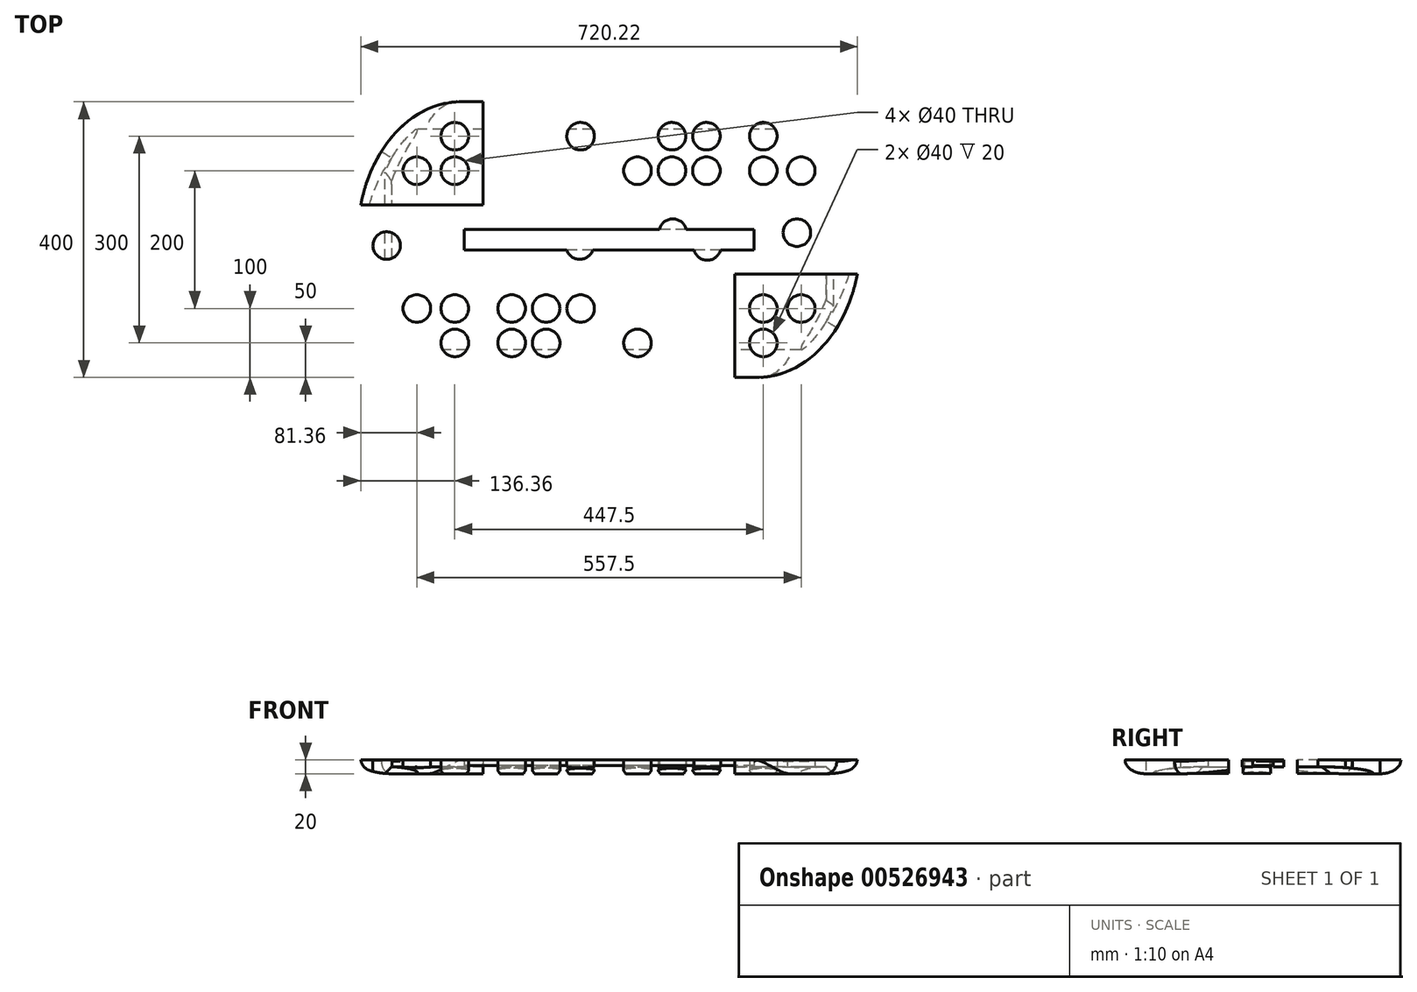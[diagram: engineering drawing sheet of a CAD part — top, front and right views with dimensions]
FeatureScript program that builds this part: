
annotation { "Feature Type Name" : "Feature", "Feature Type Description" : "" }
export const myFeature = defineFeature(function(context is Context, id is Id, definition is map)
    precondition{}
    {
        {
            var Q0;
            Q0=qCreatedBy(makeId("Top.planeOp"),FACE);
            var sketch = newSketch(context, id + "F0", { "sketchPlane" : qUnion([Q0])});
            skLineSegment(sketch, "E0.bottom", {"start": v(-365, 200) * mm, "end": v(365, 200) * mm});
            skLineSegment(sketch, "E0.top", {"start": v(-365, -200) * mm, "end": v(365, -200) * mm});
            skLineSegment(sketch, "E0.left", {"start": v(-365, 200) * mm, "end": v(-365, -200) * mm});
            skLineSegment(sketch, "E0.right", {"start": v(365, 200) * mm, "end": v(365, -200) * mm});
            skPoint(sketch, "E0.middle", {"position": v(0, 0) * mm});
            skEllipticalArc(sketch, "E1", {});
            skEllipticalArc(sketch, "E2.MirrorCS", {});
            skEllipticalArc(sketch, "E3.MirrorCS", {});
            skEllipticalArc(sketch, "E4.MirrorCS", {});
            skLineSegment(sketch, "E5", {"start": v(-365, 200) * mm, "end": v(-105, 200) * mm});
            skLineSegment(sketch, "E6", {"start": v(-365, 200) * mm, "end": v(-365, 50) * mm});
            skLineSegment(sketch, "E7", {"start": v(-365, -200) * mm, "end": v(-365, -50) * mm});
            skLineSegment(sketch, "E8", {"start": v(-365, -200) * mm, "end": v(-182.5, -200) * mm});
            skLineSegment(sketch, "E9", {"start": v(365, 200) * mm, "end": v(105, 200) * mm});
            skLineSegment(sketch, "E10", {"start": v(182.5, -200.11) * mm, "end": v(365, -200) * mm});
            skPoint(sketch, "E11", {"position": v(0, 200) * mm});
            skLineSegment(sketch, "E12", {"start": v(0, 200) * mm, "end": v(-130, 200) * mm});
            skLineSegment(sketch, "E13.MirrorCS", {"start": v(0, -200) * mm, "end": v(-130, -200) * mm});
            skLineSegment(sketch, "E14.MirrorCS", {"start": v(5, 200) * mm, "end": v(130, 200) * mm});
            skLineSegment(sketch, "E15.MirrorCS", {"start": v(-72.5, -200) * mm, "end": v(52.5, -200) * mm});
            skCircle(sketch, "E16", {"center": v(-278.75, 100) * mm, "radius": 20 * mm});
            skCircle(sketch, "E17", {"center": v(-223.75, 150) * mm, "radius": 20 * mm});
            skCircle(sketch, "E18", {"center": v(-223.75, 100) * mm, "radius": 20 * mm});
            skCircle(sketch, "E19", {"center": v(-141.25, 100) * mm, "radius": 20 * mm});
            skCircle(sketch, "E20", {"center": v(-141.25, 150) * mm, "radius": 20 * mm});
            skCircle(sketch, "E21", {"center": v(-91.25, 100) * mm, "radius": 20 * mm});
            skCircle(sketch, "E22", {"center": v(-91.25, 150) * mm, "radius": 20 * mm});
            skCircle(sketch, "E23", {"center": v(-41.25, 100) * mm, "radius": 20 * mm});
            skCircle(sketch, "E24.MirrorC", {"center": v(-41.25, 150) * mm, "radius": 20 * mm});
            skCircle(sketch, "E25.MirrorC", {"center": v(-278.75, -100) * mm, "radius": 20 * mm});
            skCircle(sketch, "E26.MirrorC", {"center": v(-223.75, -150) * mm, "radius": 20 * mm});
            skCircle(sketch, "E27.MirrorC", {"center": v(-223.75, -100) * mm, "radius": 20 * mm});
            skCircle(sketch, "E28.MirrorC", {"center": v(-141.25, -100) * mm, "radius": 20 * mm});
            skCircle(sketch, "E29.MirrorC", {"center": v(-141.25, -150) * mm, "radius": 20 * mm});
            skCircle(sketch, "E30.MirrorC", {"center": v(-91.25, -100) * mm, "radius": 20 * mm});
            skCircle(sketch, "E31.MirrorC", {"center": v(-41.25, -100) * mm, "radius": 20 * mm});
            skCircle(sketch, "E32.MirrorC", {"center": v(-91.25, -150) * mm, "radius": 20 * mm});
            skCircle(sketch, "E33.MirrorC", {"center": v(-41.25, -150) * mm, "radius": 20 * mm});
            skCircle(sketch, "E34.MirrorC", {"center": v(-222.5, -10) * mm, "radius": 20 * mm});
            skLineSegment(sketch, "E35.bottom", {"start": v(210, 15) * mm, "end": v(-210, 15) * mm});
            skLineSegment(sketch, "E35.top", {"start": v(210, -15) * mm, "end": v(-210, -15) * mm});
            skLineSegment(sketch, "E35.left", {"start": v(210, 15) * mm, "end": v(210, -15) * mm});
            skLineSegment(sketch, "E35.right", {"start": v(-210, 15) * mm, "end": v(-210, -15) * mm});
            skLineSegment(sketch, "E36", {"start": v(-365, -50) * mm, "end": v(365, -50) * mm});
            skLineSegment(sketch, "E37", {"start": v(-365, 50) * mm, "end": v(365, 50) * mm});
            skLineSegment(sketch, "E38", {"start": v(-182.5, -200) * mm, "end": v(-182.5, -40.61) * mm});
            skLineSegment(sketch, "E39", {"start": v(0, -200) * mm, "end": v(0, -50) * mm});
            skLineSegment(sketch, "E40", {"start": v(182.5, -200.11) * mm, "end": v(182.4, -40.7) * mm});
            skLineSegment(sketch, "E41.trimOffspring", {"start": v(-182.5, 40.61) * mm, "end": v(-182.5, 200) * mm});
            skLineSegment(sketch, "E42.trimOffspring", {"start": v(-182.5, -15) * mm, "end": v(-182.5, 15) * mm});
            skLineSegment(sketch, "E43.trimOffspring", {"start": v(182.39, -15) * mm, "end": v(182.37, 15) * mm});
            skLineSegment(sketch, "E44.trimOffspring", {"start": v(182.35, 40.73) * mm, "end": v(182.25, 200) * mm});
            skCircle(sketch, "E45", {"center": v(-272.5, 10) * mm, "radius": 20 * mm});
            skCircle(sketch, "E46.MirrorC", {"center": v(-322.5, -8.74) * mm, "radius": 20 * mm});
            skCircle(sketch, "E47.MirrorC", {"center": v(-142.5, -10) * mm, "radius": 20 * mm});
            skCircle(sketch, "E48.MirrorC", {"center": v(-92.5, 10) * mm, "radius": 20 * mm});
            skCircle(sketch, "E49.MirrorC", {"center": v(-42.5, -8.74) * mm, "radius": 20 * mm});
            skCircle(sketch, "E50.MirrorC", {"center": v(42.5, -8.74) * mm, "radius": 20 * mm});
            skCircle(sketch, "E51.MirrorC", {"center": v(142.5, -10) * mm, "radius": 20 * mm});
            skCircle(sketch, "E52.MirrorC", {"center": v(92.5, 10) * mm, "radius": 20 * mm});
            skCircle(sketch, "E53.MirrorC", {"center": v(222.5, -10) * mm, "radius": 20 * mm});
            skCircle(sketch, "E54.MirrorC", {"center": v(272.5, 10) * mm, "radius": 20 * mm});
            skCircle(sketch, "E55.MirrorC", {"center": v(322.5, -8.74) * mm, "radius": 20 * mm});
            skCircle(sketch, "E56.MirrorC", {"center": v(223.75, -100) * mm, "radius": 20 * mm});
            skCircle(sketch, "E57.MirrorC", {"center": v(223.75, -150) * mm, "radius": 20 * mm});
            skCircle(sketch, "E58.MirrorC", {"center": v(278.75, -100) * mm, "radius": 20 * mm});
            skCircle(sketch, "E59.MirrorC", {"center": v(141.25, -100) * mm, "radius": 20 * mm});
            skCircle(sketch, "E60.MirrorC", {"center": v(141.25, -150) * mm, "radius": 20 * mm});
            skCircle(sketch, "E61.MirrorC", {"center": v(91.25, -150) * mm, "radius": 20 * mm});
            skCircle(sketch, "E62.MirrorC", {"center": v(91.25, -100) * mm, "radius": 20 * mm});
            skCircle(sketch, "E63.MirrorC", {"center": v(41.25, -100) * mm, "radius": 20 * mm});
            skCircle(sketch, "E64.MirrorC", {"center": v(41.25, -150) * mm, "radius": 20 * mm});
            skCircle(sketch, "E65.MirrorC", {"center": v(41.25, 100) * mm, "radius": 20 * mm});
            skCircle(sketch, "E66.MirrorC", {"center": v(91.25, 100) * mm, "radius": 20 * mm});
            skCircle(sketch, "E67.MirrorC", {"center": v(141.25, 100) * mm, "radius": 20 * mm});
            skCircle(sketch, "E68.MirrorC", {"center": v(223.75, 100) * mm, "radius": 20 * mm});
            skCircle(sketch, "E69.MirrorC", {"center": v(278.75, 100) * mm, "radius": 20 * mm});
            skCircle(sketch, "E70.MirrorC", {"center": v(223.75, 150) * mm, "radius": 20 * mm});
            skCircle(sketch, "E71.MirrorC", {"center": v(141.25, 150) * mm, "radius": 20 * mm});
            skCircle(sketch, "E72.MirrorC", {"center": v(91.25, 150) * mm, "radius": 20 * mm});
            skCircle(sketch, "E73.MirrorC", {"center": v(41.25, 150) * mm, "radius": 20 * mm});
            const initialGuessF0  = {"E1": [0.215000023161019, -0.00011114199246731203, 0, -1, 0.20000000103052606, 0.15, 6.249845643425636, 1.5707963267948966], "E2.MirrorCS": [-0.215, -0.00011114199246737072, 0, -1, 0.2, 0.15, 4.711833270393751, 0.03333950926130193], "E3.MirrorCS": [-0.215, 0.00011114199246727815, 0, 1, 0.2, 0.15, 6.249845797918284, 1.5707963267948966], "E4.MirrorCS": [0.215, 0.00011114199246735796, 0, 1, 0.2, 0.15, 4.711277560231201, 0.03333950926130226]};
            skSetInitialGuess(sketch, initialGuessF0);
            skSolve(sketch);
        }
        {
            var Q0;
            Q0=qCreatedBy(makeId("Top.planeOp"),FACE);
            cPlane(context, id + "F1", {"entities" : qUnion([Q0]), "cplaneType" : CPlaneType.OFFSET, "offset" : 20 * mm, "width" : 150 * mm, "height" : 150 * mm});
        }
        {
            var Q0;
            Q0=qCreatedBy(id+"F1.planeOp",FACE);
            var sketch = newSketch(context, id + "F2", { "sketchPlane" : qUnion([Q0])});
            skLineSegment(sketch, "E74.bottom", {"start": v(0, 0) * mm, "end": v(365, 0) * mm});
            skLineSegment(sketch, "E74.top", {"start": v(0, -200) * mm, "end": v(210, -200) * mm});
            skLineSegment(sketch, "E74.left", {"start": v(0, 0) * mm, "end": v(0, -200) * mm});
            skLineSegment(sketch, "E75", {"start": v(0, -15) * mm, "end": v(364.58, -15) * mm});
            skLineSegment(sketch, "E76", {"start": v(0, -170) * mm, "end": v(294.02, -170) * mm});
            skLineSegment(sketch, "E77", {"start": v(330, 0) * mm, "end": v(330, -128.4) * mm});
            skLineSegment(sketch, "E78", {"start": v(215, 0) * mm, "end": v(215, -200) * mm});
            skPoint(sketch, "E79", {"position": v(215, -200) * mm});
            skPoint(sketch, "E80", {"position": v(365, 0) * mm});
            skLineSegment(sketch, "E81", {"start": v(275, 0) * mm, "end": v(275, -183.3) * mm});
            skLineSegment(sketch, "E82", {"start": v(275, -140) * mm, "end": v(322.12, -140) * mm});
            skPoint(sketch, "E83", {"position": v(215, -170) * mm});
            skPoint(sketch, "E84", {"position": v(330, 0) * mm});
            skPoint(sketch, "E85", {"position": v(275, -140) * mm});
            skPoint(sketch, "E86", {"position": v(330, -140) * mm});
            skPoint(sketch, "E87", {"position": v(275, -185) * mm});
            skLineSegment(sketch, "E88", {"start": v(315, -149.07) * mm, "end": v(315, 0) * mm});
            skLineSegment(sketch, "E89", {"start": v(210, 0) * mm, "end": v(210, -200) * mm});
            skEllipticalArc(sketch, "E90.trimOffspring", {});
            skEllipticalArc(sketch, "E91", {});
            skPoint(sketch, "E92.orphan", {"position": v(365, -170) * mm});
            skPoint(sketch, "E93.trimOffspring.end.orphan", {"position": v(330, -200) * mm});
            skPoint(sketch, "E94.orphan", {"position": v(365, -200) * mm});
            skPoint(sketch, "E95.orphan", {"position": v(365, -15) * mm});
            skLineSegment(sketch, "E96.MirrorCS", {"start": v(0, 0) * mm, "end": v(-365, 0) * mm});
            skLineSegment(sketch, "E97.MirrorCS", {"start": v(0, -15) * mm, "end": v(-364.58, -15) * mm});
            skLineSegment(sketch, "E98.MirrorCS", {"start": v(0, -170) * mm, "end": v(-294.02, -170) * mm});
            skLineSegment(sketch, "E99.MirrorCS", {"start": v(0, -200) * mm, "end": v(-210, -200) * mm});
            skLineSegment(sketch, "E100.MirrorCS", {"start": v(-210, 0) * mm, "end": v(-210, -200) * mm});
            skLineSegment(sketch, "E101.MirrorCS", {"start": v(-215, 0) * mm, "end": v(-215, -200) * mm});
            skEllipticalArc(sketch, "E102.MirrorCS", {});
            skEllipticalArc(sketch, "E103.MirrorCS", {});
            skLineSegment(sketch, "E104.MirrorCS", {"start": v(-275, 0) * mm, "end": v(-275, -183.3) * mm});
            skLineSegment(sketch, "E105.MirrorCS", {"start": v(-275, -140) * mm, "end": v(-322.12, -140) * mm});
            skLineSegment(sketch, "E106.MirrorCS", {"start": v(-315, -149.07) * mm, "end": v(-315, 0) * mm});
            skLineSegment(sketch, "E107.MirrorCS", {"start": v(-330, 0) * mm, "end": v(-330, -128.4) * mm});
            skLineSegment(sketch, "E108.MirrorCS", {"start": v(0, 15) * mm, "end": v(-364.58, 15) * mm});
            skLineSegment(sketch, "E109.MirrorCS", {"start": v(0, 15) * mm, "end": v(364.58, 15) * mm});
            skEllipticalArc(sketch, "E110.MirrorCS", {});
            skLineSegment(sketch, "E111.MirrorCS", {"start": v(-330, 0) * mm, "end": v(-330, 128.4) * mm});
            skLineSegment(sketch, "E112.MirrorCS", {"start": v(-315, 149.07) * mm, "end": v(-315, 0) * mm});
            skLineSegment(sketch, "E113.MirrorCS", {"start": v(-275, 0) * mm, "end": v(-275, 183.3) * mm});
            skLineSegment(sketch, "E114.MirrorCS", {"start": v(-215, 0) * mm, "end": v(-215, 200) * mm});
            skLineSegment(sketch, "E115.MirrorCS", {"start": v(-210, 0) * mm, "end": v(-210, 200) * mm});
            skLineSegment(sketch, "E116.MirrorCS", {"start": v(0, 0) * mm, "end": v(0, 200) * mm});
            skLineSegment(sketch, "E117.MirrorCS", {"start": v(210, 0) * mm, "end": v(210, 200) * mm});
            skLineSegment(sketch, "E118.MirrorCS", {"start": v(215, 0) * mm, "end": v(215, 200) * mm});
            skLineSegment(sketch, "E119.MirrorCS", {"start": v(275, 0) * mm, "end": v(275, 183.3) * mm});
            skLineSegment(sketch, "E120.MirrorCS", {"start": v(315, 149.07) * mm, "end": v(315, 0) * mm});
            skLineSegment(sketch, "E121.MirrorCS", {"start": v(330, 0) * mm, "end": v(330, 128.4) * mm});
            skEllipticalArc(sketch, "E122.MirrorCS", {});
            skEllipticalArc(sketch, "E123.MirrorCS", {});
            skEllipticalArc(sketch, "E124.MirrorCS", {});
            skLineSegment(sketch, "E125.MirrorCS", {"start": v(-275, 140) * mm, "end": v(-322.12, 140) * mm});
            skLineSegment(sketch, "E126.MirrorCS", {"start": v(0, 170) * mm, "end": v(-294.02, 170) * mm});
            skLineSegment(sketch, "E127.MirrorCS", {"start": v(0, 170) * mm, "end": v(294.02, 170) * mm});
            skLineSegment(sketch, "E128.MirrorCS", {"start": v(0, 200) * mm, "end": v(210, 200) * mm});
            skLineSegment(sketch, "E129.MirrorCS", {"start": v(0, 200) * mm, "end": v(-210, 200) * mm});
            skLineSegment(sketch, "E130.MirrorCS", {"start": v(275, 140) * mm, "end": v(322.12, 140) * mm});
            const initialGuessF2  = {"E90.trimOffspring": [0.215, 0, 1, 0, 0.115, 0.17, 4.71238898038469, 6.283185307179586], "E91": [0.215, 0, 0, -1, 0.2, 0.15, 6.249845797918284, 1.5707963267948966], "E102.MirrorCS": [-0.215, 0, -1, 0, 0.115, 0.17, 6.283185307179586, 1.5707963267948966], "E103.MirrorCS": [-0.215, 0, 0, -1, 0.2, 0.15, 4.71238898038469, 0.03333950926130225], "E110.MirrorCS": [-0.215, 0, 0, 1, 0.2, 0.15, 6.249845797918284, 1.5707963267948966], "E122.MirrorCS": [0.215, 0, 0, 1, 0.2, 0.15, 4.71238898038469, 0.03333950926130225], "E123.MirrorCS": [0.215, 0, 1, 0, 0.115, 0.17, 6.283185307179586, 1.5707963267948966], "E124.MirrorCS": [-0.215, 0, -1, 0, 0.115, 0.17, 4.71238898038469, 6.283185307179586]};
            skSetInitialGuess(sketch, initialGuessF2);
            skSolve(sketch);
        }
        {
            var Q0;
            Q0=qCreatedBy(makeId("Right.planeOp"),FACE);
            var sketch = newSketch(context, id + "F3", { "sketchPlane" : qUnion([Q0])});
            skPoint(sketch, "E131.middle", {"position": v(0, 20) * mm});
            skPoint(sketch, "E132", {"position": v(170, 0) * mm});
            skPoint(sketch, "E133", {"position": v(160, 0) * mm});
            skLineSegment(sketch, "E134.bottom", {"start": v(15, 10.07) * mm, "end": v(80, 10.07) * mm});
            skPoint(sketch, "E135", {"position": v(80, 10.07) * mm});
            skEllipticalArc(sketch, "E136", {});
            skEllipticalArc(sketch, "E137", {});
            skLineSegment(sketch, "E138", {"start": v(0, 20) * mm, "end": v(0, 10.04) * mm});
            skLineSegment(sketch, "E139", {"start": v(0, 20) * mm, "end": v(200, 20) * mm});
            skLineSegment(sketch, "E140", {"start": v(200, 20) * mm, "end": v(0, 20) * mm});
            skLineSegment(sketch, "E141", {"start": v(160, 0) * mm, "end": v(170, 0) * mm});
            skPoint(sketch, "E142.orphan", {"position": v(-200, 20) * mm});
            skLineSegment(sketch, "E143.MirrorCS", {"start": v(-200, 20) * mm, "end": v(0, 20) * mm});
            skLineSegment(sketch, "E144.MirrorCS", {"start": v(-15, 10.07) * mm, "end": v(-80, 10.07) * mm});
            skEllipticalArc(sketch, "E145.MirrorCS", {});
            skLineSegment(sketch, "E146.MirrorCS", {"start": v(-160, 0) * mm, "end": v(-170, 0) * mm});
            skEllipticalArc(sketch, "E147.MirrorCS", {});
            skLineSegment(sketch, "E148.top", {"start": v(-15, 12) * mm, "end": v(15, 12) * mm});
            skLineSegment(sketch, "E148.left", {"start": v(-15, 10.07) * mm, "end": v(-15, 12) * mm});
            skLineSegment(sketch, "E148.right", {"start": v(15, 10.07) * mm, "end": v(15, 12) * mm});
            skLineSegment(sketch, "E149.bottom", {"start": v(15, 18) * mm, "end": v(-15, 18) * mm});
            skLineSegment(sketch, "E149.top", {"start": v(15, 12) * mm, "end": v(-15, 12) * mm});
            skLineSegment(sketch, "E149.left", {"start": v(15, 18) * mm, "end": v(15, 12) * mm});
            skLineSegment(sketch, "E149.right", {"start": v(-15, 18) * mm, "end": v(-15, 12) * mm});
            skLineSegment(sketch, "E150", {"start": v(170, 0) * mm, "end": v(170.12, 20) * mm});
            skLineSegment(sketch, "E151", {"start": v(-170, 0) * mm, "end": v(-170.12, 20) * mm});
            skLineSegment(sketch, "E152", {"start": v(-15, 12) * mm, "end": v(-15, 10.07) * mm});
            skLineSegment(sketch, "E153.bottom", {"start": v(-200, 20) * mm, "end": v(-170, 20) * mm});
            skLineSegment(sketch, "E153.top", {"start": v(-200, 0) * mm, "end": v(-170, 0) * mm});
            skLineSegment(sketch, "E153.left", {"start": v(-200, 20) * mm, "end": v(-200, 0) * mm});
            skLineSegment(sketch, "E153.right", {"start": v(-170, 20) * mm, "end": v(-170, 0) * mm});
            skLineSegment(sketch, "E154.MirrorCS", {"start": v(200, 0) * mm, "end": v(170, 0) * mm});
            skLineSegment(sketch, "E155.MirrorCS", {"start": v(200, 20) * mm, "end": v(200, 0) * mm});
            skLineSegment(sketch, "E156", {"start": v(80, 10.07) * mm, "end": v(80, 20) * mm});
            skLineSegment(sketch, "E157", {"start": v(160, 0) * mm, "end": v(160, 20) * mm});
            skLineSegment(sketch, "E158", {"start": v(149.2, 20) * mm, "end": v(149.2, 5.05) * mm});
            skLineSegment(sketch, "E159", {"start": v(140.08, 20) * mm, "end": v(140.08, 6.65) * mm});
            skLineSegment(sketch, "E160", {"start": v(128.23, 20) * mm, "end": v(128.23, 8.04) * mm});
            skLineSegment(sketch, "E161", {"start": v(102.69, 20) * mm, "end": v(102.69, 9.66) * mm});
            skLineSegment(sketch, "E162.MirrorCS", {"start": v(-80, 10.07) * mm, "end": v(-80, 20) * mm});
            skLineSegment(sketch, "E163.MirrorCS", {"start": v(-102.69, 20) * mm, "end": v(-102.69, 9.66) * mm});
            skLineSegment(sketch, "E164.MirrorCS", {"start": v(-128.23, 20) * mm, "end": v(-128.23, 8.04) * mm});
            skLineSegment(sketch, "E165.MirrorCS", {"start": v(-140.08, 20) * mm, "end": v(-140.08, 6.65) * mm});
            skLineSegment(sketch, "E166.MirrorCS", {"start": v(-149.2, 20) * mm, "end": v(-149.2, 5.05) * mm});
            skLineSegment(sketch, "E167.MirrorCS", {"start": v(-160, 0) * mm, "end": v(-160, 20) * mm});
            skLineSegment(sketch, "E168", {"start": v(45, 20) * mm, "end": v(45, 10.07) * mm});
            skLineSegment(sketch, "E169.MirrorCS", {"start": v(-45, 20) * mm, "end": v(-45, 10.07) * mm});
            const initialGuessF3  = {"E136": [0.17012490332126617, 0.02, -0.006245044279577429, -0.9999804995208388, 0.020000390017188747, 0.02987581400604767, 6.283185307179586, 1.580124845260153], "E137": [0.08, 0, 0, 1, 0.01007139225942586, 0.08, 4.71238898038469, 6.283185307179586], "E145.MirrorCS": [-0.08, 0, 0, 1, 0.01007139225942586, 0.08, 6.283185307179586, 1.5707963267948966], "E147.MirrorCS": [-0.17012490332126617, 0.02, 0.006245044279579518, -0.9999804995208388, 0.020000390017188747, 0.02987581400604767, 4.703060461919433, 6.283185307179586]};
            skSetInitialGuess(sketch, initialGuessF3);
            skSolve(sketch);
        }
        {
            var Q0;
            Q0=qCreatedBy(makeId("Front.planeOp"),FACE);
            var sketch = newSketch(context, id + "F4", { "sketchPlane" : qUnion([Q0])});
            skLineSegment(sketch, "E170", {"start": v(0, 20) * mm, "end": v(365, 20) * mm});
            skPoint(sketch, "E171", {"position": v(210, 20) * mm});
            skLineSegment(sketch, "E172", {"start": v(210, 18) * mm, "end": v(210, 12) * mm});
            skPoint(sketch, "E173", {"position": v(315, 20) * mm});
            skLineSegment(sketch, "E174", {"start": v(315, 18) * mm, "end": v(315, 0) * mm});
            skLineSegment(sketch, "E175", {"start": v(0, 12) * mm, "end": v(0, 20) * mm});
            skLineSegment(sketch, "E176", {"start": v(210, 12) * mm, "end": v(0, 12) * mm});
            skPoint(sketch, "E177", {"position": v(365.07, 0) * mm});
            skPoint(sketch, "E178", {"position": v(365, 20) * mm});
            skEllipticalArc(sketch, "E179", {});
            skLineSegment(sketch, "E180", {"start": v(315, 18) * mm, "end": v(210, 18) * mm});
            skLineSegment(sketch, "E181.MirrorCS", {"start": v(0, 20) * mm, "end": v(-365, 20) * mm});
            skLineSegment(sketch, "E182.MirrorCS", {"start": v(-210, 12) * mm, "end": v(0, 12) * mm});
            skLineSegment(sketch, "E183.MirrorCS", {"start": v(-210, 18) * mm, "end": v(-210, 12) * mm});
            skLineSegment(sketch, "E184.MirrorCS", {"start": v(-315, 18) * mm, "end": v(-210, 18) * mm});
            skLineSegment(sketch, "E185.MirrorCS", {"start": v(-315, 18) * mm, "end": v(-315, 0) * mm});
            skEllipticalArc(sketch, "E186.MirrorCS", {});
            skPoint(sketch, "E187", {"position": v(245, 20) * mm});
            skPoint(sketch, "E188", {"position": v(245, 10.07) * mm});
            skPoint(sketch, "E189", {"position": v(325, 20) * mm});
            skPoint(sketch, "E190", {"position": v(335, 20) * mm});
            skLineSegment(sketch, "E191", {"start": v(335, 20) * mm, "end": v(335, 10.07) * mm});
            skLineSegment(sketch, "E192", {"start": v(335, 10.07) * mm, "end": v(0, 10.07) * mm});
            skLineSegment(sketch, "E193.MirrorCS", {"start": v(-335, 10.07) * mm, "end": v(0, 10.07) * mm});
            skLineSegment(sketch, "E194.MirrorCS", {"start": v(-335, 20) * mm, "end": v(-335, 10.07) * mm});
            skLineSegment(sketch, "E195", {"start": v(365, 20) * mm, "end": v(365.07, 0) * mm});
            skLineSegment(sketch, "E196", {"start": v(315, 0) * mm, "end": v(365.07, 0) * mm});
            skLineSegment(sketch, "E197.MirrorCS", {"start": v(-365, 20) * mm, "end": v(-365.07, 0) * mm});
            skLineSegment(sketch, "E198.MirrorCS", {"start": v(-315, 0) * mm, "end": v(-365.07, 0) * mm});
            skLineSegment(sketch, "E199", {"start": v(335, 10.07) * mm, "end": v(335, 1.67) * mm});
            skLineSegment(sketch, "E200.MirrorCS", {"start": v(-335, 10.07) * mm, "end": v(-335, 1.67) * mm});
            skLineSegment(sketch, "E201", {"start": v(-315, 18) * mm, "end": v(-315, 20) * mm});
            skLineSegment(sketch, "E202", {"start": v(-210, 18) * mm, "end": v(-210, 20) * mm});
            skLineSegment(sketch, "E203.MirrorCS", {"start": v(210, 18) * mm, "end": v(210, 20) * mm});
            skLineSegment(sketch, "E204.MirrorCS", {"start": v(315, 18) * mm, "end": v(315, 20) * mm});
            skPoint(sketch, "E205", {"position": v(275, 20) * mm});
            skPoint(sketch, "E206.MirrorP", {"position": v(-275, 20) * mm});
            skLineSegment(sketch, "E207", {"start": v(275, 20) * mm, "end": v(275, 18) * mm});
            skLineSegment(sketch, "E208.MirrorCS", {"start": v(-275, 20) * mm, "end": v(-275, 18) * mm});
            skPoint(sketch, "E209", {"position": v(-333.25, 14.9) * mm});
            skPoint(sketch, "E210", {"position": v(-218.12, 14.9) * mm});
            skPoint(sketch, "E211", {"position": v(-78.75, 14.9) * mm});
            const initialGuessF4  = {"E179": [0.315, 0.02, 1, 0, 0.05, 0.02, 4.71238898038469, 0], "E186.MirrorCS": [-0.315, 0.02, -1, 0, 0.05, 0.02, 0, 1.5707963267948966]};
            skSetInitialGuess(sketch, initialGuessF4);
            skSolve(sketch);
        }
        {
            var Q0;
            Q0 = qSketchRegion(id + "F2", true);
            var Q1;
            {var subQ0=sQuery(id+"F2.wireOp",EDGE,"E125.MirrorCS");var subQ1=sQuery(id+"F2.wireOp",EDGE,"E112.MirrorCS");var subQ2=makeQuery(id+"F2.imprint","INTERSECT",VERTEX,{"derivedFrom":[subQ1,subQ0]});Q1=makeQuery(id+"F2.imprint","IMPRINT",FACE,{"disambiguationData":[TD([[makeQuery(id+"F2.imprint","IMPRINT",EDGE,{"disambiguationData":[TD([[subQ2,-1.0]])],"derivedFrom":subQ1}),1.0]])]});}
            var Q2;
            {var subQ0=sQuery(id+"F2.wireOp",EDGE,"E124.MirrorCS");var subQ1=sQuery(id+"F2.wireOp",EDGE,"E113.MirrorCS");var subQ2=makeQuery(id+"F2.imprint","INTERSECT",VERTEX,{"derivedFrom":[subQ1,subQ0]});Q2=makeQuery(id+"F2.imprint","IMPRINT",FACE,{"disambiguationData":[TD([[makeQuery(id+"F2.imprint","IMPRINT",EDGE,{"disambiguationData":[TD([[subQ2,-1.0]])],"derivedFrom":subQ1}),-1.0]])]});}
            var Q3;
            {var subQ0=sQuery(id+"F2.wireOp",EDGE,"E123.MirrorCS");var subQ1=sQuery(id+"F2.wireOp",EDGE,"E119.MirrorCS");var subQ2=makeQuery(id+"F2.imprint","INTERSECT",VERTEX,{"derivedFrom":[subQ1,subQ0]});Q3=makeQuery(id+"F2.imprint","IMPRINT",FACE,{"disambiguationData":[TD([[makeQuery(id+"F2.imprint","IMPRINT",EDGE,{"disambiguationData":[TD([[subQ2,-1.0]])],"derivedFrom":subQ1}),1.0]])]});}
            var Q4;
            {var subQ0=sQuery(id+"F2.wireOp",EDGE,"E130.MirrorCS");var subQ1=sQuery(id+"F2.wireOp",EDGE,"E120.MirrorCS");var subQ2=makeQuery(id+"F2.imprint","INTERSECT",VERTEX,{"derivedFrom":[subQ1,subQ0]});Q4=makeQuery(id+"F2.imprint","IMPRINT",FACE,{"disambiguationData":[TD([[makeQuery(id+"F2.imprint","IMPRINT",EDGE,{"disambiguationData":[TD([[subQ2,-1.0]])],"derivedFrom":subQ1}),-1.0]])]});}
            var Q5;
            {var subQ0=sQuery(id+"F2.wireOp",EDGE,"E90.trimOffspring");var subQ1=sQuery(id+"F2.wireOp",EDGE,"E82");var subQ2=makeQuery(id+"F2.imprint","INTERSECT",VERTEX,{"derivedFrom":[subQ1,subQ0]});Q5=makeQuery(id+"F2.imprint","IMPRINT",FACE,{"disambiguationData":[TD([[makeQuery(id+"F2.imprint","IMPRINT",EDGE,{"disambiguationData":[TD([[subQ2,-1.0]])],"derivedFrom":subQ1}),1.0]])]});}
            var Q6;
            {var subQ1=sQuery(id+"F2.wireOp",EDGE,"E76");var subQ3=sQuery(id+"F2.wireOp",EDGE,"E81");var subQ4=makeQuery(id+"F2.imprint","INTERSECT",VERTEX,{"derivedFrom":[subQ1,subQ3]});Q6=makeQuery(id+"F2.imprint","IMPRINT",FACE,{"disambiguationData":[TD([[makeQuery(id+"F2.imprint","IMPRINT",EDGE,{"disambiguationData":[TD([[subQ4,1.0]])],"derivedFrom":subQ3}),-1.0]])]});}
            var Q7;
            {var subQ1=sQuery(id+"F2.wireOp",EDGE,"E98.MirrorCS");var subQ3=sQuery(id+"F2.wireOp",EDGE,"E104.MirrorCS");var subQ4=makeQuery(id+"F2.imprint","INTERSECT",VERTEX,{"derivedFrom":[subQ1,subQ3]});Q7=makeQuery(id+"F2.imprint","IMPRINT",FACE,{"disambiguationData":[TD([[makeQuery(id+"F2.imprint","IMPRINT",EDGE,{"disambiguationData":[TD([[subQ4,1.0]])],"derivedFrom":subQ3}),1.0]])]});}
            var Q8;
            {var subQ0=sQuery(id+"F2.wireOp",EDGE,"E106.MirrorCS");var subQ1=sQuery(id+"F2.wireOp",EDGE,"E102.MirrorCS");var subQ2=makeQuery(id+"F2.imprint","INTERSECT",VERTEX,{"derivedFrom":[subQ1,subQ0]});Q8=makeQuery(id+"F2.imprint","IMPRINT",FACE,{"disambiguationData":[TD([[makeQuery(id+"F2.imprint","IMPRINT",EDGE,{"disambiguationData":[TD([[subQ2,-1.0]])],"derivedFrom":subQ1}),-1.0]])]});}
            extrude(context, id + "F5", {"entities" : qUnion([Q0, Q1, Q2, Q3, Q4, Q5, Q6, Q7, Q8]), "oppositeDirection" : true, "depth" : 20 * mm, "offsetDistance" : 25 * mm});
        }
        {
            var Q0;
            {var subQ0=sQuery(id+"F3.wireOp",EDGE,"E149.right");Q0=makeQuery(id+"F3.imprint","IMPRINT",FACE,{"disambiguationData":[TD([[makeQuery(id+"F3.imprint","IMPRINT",EDGE,{"derivedFrom":subQ0}),-1.0]])]});}
            var Q1;
            {var subQ0=sQuery(id+"F3.wireOp",EDGE,"E149.left");Q1=makeQuery(id+"F3.imprint","IMPRINT",FACE,{"disambiguationData":[TD([[makeQuery(id+"F3.imprint","IMPRINT",EDGE,{"derivedFrom":subQ0}),1.0]])]});}
            extrude(context, id + "F6", {"entities" : qUnion([Q0, Q1]), "operationType" : NewBodyOperationType.ADD, "depth" : 420 * mm, "offsetDistance" : 25 * mm, "symmetric" : true});
        }
        {
            var Q0;
            {var subQ0=sQuery(id+"F3.wireOp",EDGE,"E156");Q0=makeQuery(id+"F3.imprint","IMPRINT",FACE,{"disambiguationData":[TD([[makeQuery(id+"F3.imprint","IMPRINT",EDGE,{"derivedFrom":subQ0}),-1.0]])]});}
            var Q1;
            {var subQ0=sQuery(id+"F3.wireOp",EDGE,"E160");Q1=makeQuery(id+"F3.imprint","IMPRINT",FACE,{"disambiguationData":[TD([[makeQuery(id+"F3.imprint","IMPRINT",EDGE,{"derivedFrom":subQ0}),-1.0]])]});}
            var Q2;
            {var subQ0=sQuery(id+"F3.wireOp",EDGE,"E159");Q2=makeQuery(id+"F3.imprint","IMPRINT",FACE,{"disambiguationData":[TD([[makeQuery(id+"F3.imprint","IMPRINT",EDGE,{"derivedFrom":subQ0}),-1.0]])]});}
            var Q3;
            {var subQ0=sQuery(id+"F3.wireOp",EDGE,"E158");Q3=makeQuery(id+"F3.imprint","IMPRINT",FACE,{"disambiguationData":[TD([[makeQuery(id+"F3.imprint","IMPRINT",EDGE,{"derivedFrom":subQ0}),-1.0]])]});}
            var Q4;
            {var subQ0=sQuery(id+"F3.wireOp",EDGE,"E157");Q4=makeQuery(id+"F3.imprint","IMPRINT",FACE,{"disambiguationData":[TD([[makeQuery(id+"F3.imprint","IMPRINT",EDGE,{"derivedFrom":subQ0}),1.0]])]});}
            var Q5;
            Q5=makeQuery(id+"F3.imprint","IMPRINT",FACE,{"disambiguationData":[TD([[makeQuery(id+"F3.imprint","IMPRINT",EDGE,{"derivedFrom":sQuery(id+"F3.wireOp",EDGE,"E141")}),1.0]])]});
            var Q6;
            {var subQ0=sQuery(id+"F3.wireOp",EDGE,"E162.MirrorCS");Q6=makeQuery(id+"F3.imprint","IMPRINT",FACE,{"disambiguationData":[TD([[makeQuery(id+"F3.imprint","IMPRINT",EDGE,{"derivedFrom":subQ0}),1.0]])]});}
            var Q7;
            {var subQ0=sQuery(id+"F3.wireOp",EDGE,"E163.MirrorCS");Q7=makeQuery(id+"F3.imprint","IMPRINT",FACE,{"disambiguationData":[TD([[makeQuery(id+"F3.imprint","IMPRINT",EDGE,{"derivedFrom":subQ0}),-1.0]])]});}
            var Q8;
            {var subQ0=sQuery(id+"F3.wireOp",EDGE,"E164.MirrorCS");Q8=makeQuery(id+"F3.imprint","IMPRINT",FACE,{"disambiguationData":[TD([[makeQuery(id+"F3.imprint","IMPRINT",EDGE,{"derivedFrom":subQ0}),-1.0]])]});}
            var Q9;
            {var subQ0=sQuery(id+"F3.wireOp",EDGE,"E165.MirrorCS");Q9=makeQuery(id+"F3.imprint","IMPRINT",FACE,{"disambiguationData":[TD([[makeQuery(id+"F3.imprint","IMPRINT",EDGE,{"derivedFrom":subQ0}),-1.0]])]});}
            var Q10;
            {var subQ0=sQuery(id+"F3.wireOp",EDGE,"E166.MirrorCS");Q10=makeQuery(id+"F3.imprint","IMPRINT",FACE,{"disambiguationData":[TD([[makeQuery(id+"F3.imprint","IMPRINT",EDGE,{"derivedFrom":subQ0}),-1.0]])]});}
            var Q11;
            Q11=makeQuery(id+"F3.imprint","IMPRINT",FACE,{"disambiguationData":[TD([[makeQuery(id+"F3.imprint","IMPRINT",EDGE,{"derivedFrom":sQuery(id+"F3.wireOp",EDGE,"E146.MirrorCS")}),-1.0]])]});
            var Q12;
            {var subQ0=sQuery(id+"F3.wireOp",EDGE,"E156");Q12=makeQuery(id+"F3.imprint","IMPRINT",FACE,{"disambiguationData":[TD([[makeQuery(id+"F3.imprint","IMPRINT",EDGE,{"derivedFrom":subQ0}),1.0]])]});}
            var Q13;
            {var subQ0=sQuery(id+"F3.wireOp",EDGE,"E162.MirrorCS");Q13=makeQuery(id+"F3.imprint","IMPRINT",FACE,{"disambiguationData":[TD([[makeQuery(id+"F3.imprint","IMPRINT",EDGE,{"derivedFrom":subQ0}),-1.0]])]});}
            extrude(context, id + "F7", {"entities" : qUnion([Q0, Q1, Q2, Q3, Q4, Q5, Q6, Q7, Q8, Q9, Q10, Q11, Q12, Q13]), "operationType" : NewBodyOperationType.ADD, "depth" : 520 * mm, "offsetDistance" : 25 * mm, "symmetric" : true});
        }
        {
            var Q0;
            Q0=makeQuery(id+"F4.imprint","IMPRINT",FACE,{"disambiguationData":[TD([[makeQuery(id+"F4.imprint","IMPRINT",EDGE,{"derivedFrom":sQuery(id+"F4.wireOp",EDGE,"E172")}),-1.0]])]});
            var Q1;
            {var subQ1=sQuery(id+"F4.wireOp",EDGE,"E179");Q1=makeQuery(id+"F4.imprint","IMPRINT",FACE,{"disambiguationData":[TD([[makeQuery(id+"F4.imprint","IMPRINT",EDGE,{"derivedFrom":subQ1}),1.0]])]});}
            var Q2;
            {var subQ2=sQuery(id+"F4.wireOp",EDGE,"E175");Q2=makeQuery(id+"F4.imprint","IMPRINT",FACE,{"disambiguationData":[TD([[makeQuery(id+"F4.imprint","IMPRINT",EDGE,{"derivedFrom":subQ2}),1.0]])]});}
            var Q3;
            {var subQ0=sQuery(id+"F4.wireOp",EDGE,"E186.MirrorCS");Q3=makeQuery(id+"F4.imprint","IMPRINT",FACE,{"disambiguationData":[TD([[makeQuery(id+"F4.imprint","IMPRINT",EDGE,{"derivedFrom":subQ0}),1.0]])]});}
            extrude(context, id + "F8", {"entities" : qUnion([Q0, Q1, Q2, Q3]), "operationType" : NewBodyOperationType.ADD, "depth" : 30 * mm, "offsetDistance" : 25 * mm, "symmetric" : true});
        }
        {
            var Q0;
            {var subQ0=sQuery(id+"F3.wireOp",EDGE,"E153.left");var subQ1=sQuery(id+"F3.wireOp",EDGE,"E147.MirrorCS");var subQ2=makeQuery(id+"F3.imprint","INTERSECT",VERTEX,{"derivedFrom":[subQ1,subQ0]});Q0=makeQuery(id+"F3.imprint","IMPRINT",FACE,{"disambiguationData":[TD([[makeQuery(id+"F3.imprint","IMPRINT",EDGE,{"disambiguationData":[TD([[subQ2,-1.0]])],"derivedFrom":subQ1}),-1.0]])]});}
            var Q1;
            {var subQ0=sQuery(id+"F3.wireOp",EDGE,"E155.MirrorCS");var subQ1=sQuery(id+"F3.wireOp",EDGE,"E136");var subQ2=makeQuery(id+"F3.imprint","INTERSECT",VERTEX,{"derivedFrom":[subQ1,subQ0]});Q1=makeQuery(id+"F3.imprint","IMPRINT",FACE,{"disambiguationData":[TD([[makeQuery(id+"F3.imprint","IMPRINT",EDGE,{"disambiguationData":[TD([[subQ2,1.0]])],"derivedFrom":subQ1}),-1.0]])]});}
            var Q2;
            Q2=sQuery(id+"F3.wireOp",EDGE,"E153.left");
            var Q3;
            Q3=sQuery(id+"F3.wireOp",EDGE,"E153.top");
            var Q4;
            Q4=sQuery(id+"F3.wireOp",EDGE,"E147.MirrorCS");
            extrude(context, id + "F9", {"entities" : qUnion([Q0, Q1]), "operationType" : NewBodyOperationType.REMOVE, "surfaceEntities" : qUnion([Q2, Q3, Q4]), "oppositeDirection" : true, "depth" : 730 * mm, "offsetDistance" : 25 * mm, "symmetric" : true});
        }
        {
            var Q0;
            Q0=makeQuery(id+"F4.imprint","IMPRINT",FACE,{"disambiguationData":[TD([[makeQuery(id+"F4.imprint","IMPRINT",EDGE,{"derivedFrom":sQuery(id+"F4.wireOp",EDGE,"E186.MirrorCS")}),-1.0]])]});
            var Q1;
            Q1=makeQuery(id+"F4.imprint","IMPRINT",FACE,{"disambiguationData":[TD([[makeQuery(id+"F4.imprint","IMPRINT",EDGE,{"derivedFrom":sQuery(id+"F4.wireOp",EDGE,"E179")}),-1.0]])]});
            extrude(context, id + "F10", {"entities" : qUnion([Q0, Q1]), "operationType" : NewBodyOperationType.REMOVE, "oppositeDirection" : true, "depth" : 400 * mm, "offsetDistance" : 25 * mm, "symmetric" : true});
        }
        {
            var Q0;
            Q0=makeQuery(id+"F4.imprint","IMPRINT",FACE,{"disambiguationData":[TD([[makeQuery(id+"F4.imprint","IMPRINT",EDGE,{"derivedFrom":sQuery(id+"F4.wireOp",EDGE,"E172")}),-1.0]])]});
            var Q1;
            {var subQ5=sQuery(id+"F4.wireOp",EDGE,"E199");Q1=makeQuery(id+"F4.imprint","IMPRINT",FACE,{"disambiguationData":[TD([[makeQuery(id+"F4.imprint","IMPRINT",EDGE,{"derivedFrom":subQ5}),-1.0]])]});}
            var Q2;
            {var subQ5=sQuery(id+"F4.wireOp",EDGE,"E200.MirrorCS");Q2=makeQuery(id+"F4.imprint","IMPRINT",FACE,{"disambiguationData":[TD([[makeQuery(id+"F4.imprint","IMPRINT",EDGE,{"derivedFrom":subQ5}),1.0]])]});}
            var Q3;
            {var subQ2=sQuery(id+"F4.wireOp",EDGE,"E175");Q3=makeQuery(id+"F4.imprint","IMPRINT",FACE,{"disambiguationData":[TD([[makeQuery(id+"F4.imprint","IMPRINT",EDGE,{"derivedFrom":subQ2}),1.0]])]});}
            var Q4;
            {var subQ0=sQuery(id+"F4.wireOp",EDGE,"E194.MirrorCS");Q4=makeQuery(id+"F4.imprint","IMPRINT",FACE,{"disambiguationData":[TD([[makeQuery(id+"F4.imprint","IMPRINT",EDGE,{"derivedFrom":subQ0}),1.0]])]});}
            var Q5;
            {var subQ1=sQuery(id+"F4.wireOp",EDGE,"E191");Q5=makeQuery(id+"F4.imprint","IMPRINT",FACE,{"disambiguationData":[TD([[makeQuery(id+"F4.imprint","IMPRINT",EDGE,{"derivedFrom":subQ1}),-1.0]])]});}
            extrude(context, id + "F11", {"entities" : qUnion([Q0, Q1, Q2, Q3, Q4, Q5]), "operationType" : NewBodyOperationType.ADD, "depth" : 169 * mm, "offsetDistance" : 25 * mm, "symmetric" : true});
        }
        {
            var Q0;
            Q0=makeQuery(id+"F4.imprint","IMPRINT",FACE,{"disambiguationData":[TD([[makeQuery(id+"F4.imprint","IMPRINT",EDGE,{"derivedFrom":sQuery(id+"F4.wireOp",EDGE,"E180")}),-1.0]])]});
            var Q1;
            Q1=makeQuery(id+"F4.imprint","IMPRINT",FACE,{"disambiguationData":[TD([[makeQuery(id+"F4.imprint","IMPRINT",EDGE,{"derivedFrom":sQuery(id+"F4.wireOp",EDGE,"E184.MirrorCS")}),1.0]])]});
            extrude(context, id + "F12", {"entities" : qUnion([Q0, Q1]), "operationType" : NewBodyOperationType.ADD, "depth" : 295 * mm, "offsetDistance" : 25 * mm, "symmetric" : true});
        }
        {
            var Q0;
            {var subQ0=sQuery(id+"F4.wireOp",EDGE,"E203.MirrorCS");Q0=makeQuery(id+"F4.imprint","IMPRINT",FACE,{"disambiguationData":[TD([[makeQuery(id+"F4.imprint","IMPRINT",EDGE,{"derivedFrom":subQ0}),-1.0]])]});}
            var Q1;
            {var subQ0=sQuery(id+"F4.wireOp",EDGE,"E202");Q1=makeQuery(id+"F4.imprint","IMPRINT",FACE,{"disambiguationData":[TD([[makeQuery(id+"F4.imprint","IMPRINT",EDGE,{"derivedFrom":subQ0}),1.0]])]});}
            extrude(context, id + "F13", {"entities" : qUnion([Q0, Q1]), "operationType" : NewBodyOperationType.ADD, "depth" : 350 * mm, "offsetDistance" : 25 * mm, "symmetric" : true});
        }
        {
            var Q0;
            {var subQ0=sQuery(id+"F2.wireOp",EDGE,"E122.MirrorCS");var subQ1=sQuery(id+"F2.wireOp",EDGE,"E91");Q0=makeQuery(id+"F10.boolean.opBoolean","SPLIT",EDGE,{"disambiguationData":[TD([makeQuery(id+"F9.boolean.opBoolean","COPY",FACE,{"derivedFrom":makeQuery(id+"F9.opExtrude","SWEPT_FACE",FACE,{"disambiguationData":[OSD([sQuery(id+"F3.wireOp",EDGE,"E136")])]})})])],"derivedFrom":makeQuery(id+"F5.opExtrude","CAP_EDGE",EDGE,{"disambiguationData":[OSD([subQ1,subQ0])],"isStart":false})});}
            var Q1;
            {var subQ0=sQuery(id+"F2.wireOp",EDGE,"E122.MirrorCS");var subQ1=sQuery(id+"F2.wireOp",EDGE,"E91");Q1=makeQuery(id+"F10.boolean.opBoolean","SPLIT",EDGE,{"disambiguationData":[TD([makeQuery(id+"F9.boolean.opBoolean","COPY",FACE,{"derivedFrom":makeQuery(id+"F9.opExtrude","SWEPT_FACE",FACE,{"disambiguationData":[OSD([sQuery(id+"F3.wireOp",EDGE,"E147.MirrorCS")])]})})])],"derivedFrom":makeQuery(id+"F5.opExtrude","CAP_EDGE",EDGE,{"disambiguationData":[OSD([subQ1,subQ0])],"isStart":false})});}
            var Q2;
            {var subQ0=sQuery(id+"F2.wireOp",EDGE,"E110.MirrorCS");var subQ1=sQuery(id+"F2.wireOp",EDGE,"E103.MirrorCS");Q2=makeQuery(id+"F10.boolean.opBoolean","SPLIT",EDGE,{"disambiguationData":[TD([makeQuery(id+"F9.boolean.opBoolean","COPY",FACE,{"derivedFrom":makeQuery(id+"F9.opExtrude","SWEPT_FACE",FACE,{"disambiguationData":[OSD([sQuery(id+"F3.wireOp",EDGE,"E147.MirrorCS")])]})})])],"derivedFrom":makeQuery(id+"F5.opExtrude","CAP_EDGE",EDGE,{"disambiguationData":[OSD([subQ1,subQ0])],"isStart":false})});}
            var Q3;
            {var subQ0=sQuery(id+"F2.wireOp",EDGE,"E110.MirrorCS");var subQ1=sQuery(id+"F2.wireOp",EDGE,"E103.MirrorCS");Q3=makeQuery(id+"F10.boolean.opBoolean","SPLIT",EDGE,{"disambiguationData":[TD([makeQuery(id+"F9.boolean.opBoolean","COPY",FACE,{"derivedFrom":makeQuery(id+"F9.opExtrude","SWEPT_FACE",FACE,{"disambiguationData":[OSD([sQuery(id+"F3.wireOp",EDGE,"E136")])]})})])],"derivedFrom":makeQuery(id+"F5.opExtrude","CAP_EDGE",EDGE,{"disambiguationData":[OSD([subQ1,subQ0])],"isStart":false})});}
            fillet(context, id + "F14", {"entities" : qUnion([Q0, Q1, Q2, Q3]), "radius" : 18 * mm, "tangentPropagation" : true, "allowEdgeOverflow" : false});
        }
        {
            var Q0;
            {var subQ0=sQuery(id+"F3.wireOp",EDGE,"E162.MirrorCS");Q0=makeQuery(id+"F3.imprint","IMPRINT",FACE,{"disambiguationData":[TD([[makeQuery(id+"F3.imprint","IMPRINT",EDGE,{"derivedFrom":subQ0}),-1.0]])]});}
            var Q1;
            {var subQ0=sQuery(id+"F3.wireOp",EDGE,"E156");Q1=makeQuery(id+"F3.imprint","IMPRINT",FACE,{"disambiguationData":[TD([[makeQuery(id+"F3.imprint","IMPRINT",EDGE,{"derivedFrom":subQ0}),1.0]])]});}
            extrude(context, id + "F15", {"entities" : qUnion([Q0, Q1]), "operationType" : NewBodyOperationType.ADD, "depth" : 670 * mm, "offsetDistance" : 25 * mm, "symmetric" : true});
        }
        {
            var Q0;
            {var subQ0=sQuery(id+"F3.wireOp",EDGE,"E156");Q0=makeQuery(id+"F3.imprint","IMPRINT",FACE,{"disambiguationData":[TD([[makeQuery(id+"F3.imprint","IMPRINT",EDGE,{"derivedFrom":subQ0}),-1.0]])]});}
            var Q1;
            {var subQ0=sQuery(id+"F3.wireOp",EDGE,"E162.MirrorCS");Q1=makeQuery(id+"F3.imprint","IMPRINT",FACE,{"disambiguationData":[TD([[makeQuery(id+"F3.imprint","IMPRINT",EDGE,{"derivedFrom":subQ0}),1.0]])]});}
            extrude(context, id + "F16", {"entities" : qUnion([Q0, Q1]), "operationType" : NewBodyOperationType.ADD, "depth" : 630 * mm, "offsetDistance" : 25 * mm, "symmetric" : true});
        }
        {
            var Q0;
            {var subQ0=sQuery(id+"F3.wireOp",EDGE,"E166.MirrorCS");Q0=makeQuery(id+"F3.imprint","IMPRINT",FACE,{"disambiguationData":[TD([[makeQuery(id+"F3.imprint","IMPRINT",EDGE,{"derivedFrom":subQ0}),-1.0]])]});}
            var Q1;
            {var subQ0=sQuery(id+"F3.wireOp",EDGE,"E157");Q1=makeQuery(id+"F3.imprint","IMPRINT",FACE,{"disambiguationData":[TD([[makeQuery(id+"F3.imprint","IMPRINT",EDGE,{"derivedFrom":subQ0}),1.0]])]});}
            extrude(context, id + "F17", {"entities" : qUnion([Q0, Q1]), "operationType" : NewBodyOperationType.ADD, "depth" : 550 * mm, "offsetDistance" : 25 * mm, "symmetric" : true});
        }
        {
            var Q0;
            {var subQ0=sQuery(id+"F3.wireOp",EDGE,"E158");Q0=makeQuery(id+"F3.imprint","IMPRINT",FACE,{"disambiguationData":[TD([[makeQuery(id+"F3.imprint","IMPRINT",EDGE,{"derivedFrom":subQ0}),-1.0]])]});}
            var Q1;
            {var subQ0=sQuery(id+"F3.wireOp",EDGE,"E165.MirrorCS");Q1=makeQuery(id+"F3.imprint","IMPRINT",FACE,{"disambiguationData":[TD([[makeQuery(id+"F3.imprint","IMPRINT",EDGE,{"derivedFrom":subQ0}),-1.0]])]});}
            extrude(context, id + "F18", {"entities" : qUnion([Q0, Q1]), "operationType" : NewBodyOperationType.ADD, "depth" : 600 * mm, "offsetDistance" : 25 * mm, "symmetric" : true});
        }
        {
            var Q0;
            {var subQ0=sQuery(id+"F3.wireOp",EDGE,"E159");Q0=makeQuery(id+"F3.imprint","IMPRINT",FACE,{"disambiguationData":[TD([[makeQuery(id+"F3.imprint","IMPRINT",EDGE,{"derivedFrom":subQ0}),-1.0]])]});}
            var Q1;
            {var subQ0=sQuery(id+"F3.wireOp",EDGE,"E164.MirrorCS");Q1=makeQuery(id+"F3.imprint","IMPRINT",FACE,{"disambiguationData":[TD([[makeQuery(id+"F3.imprint","IMPRINT",EDGE,{"derivedFrom":subQ0}),-1.0]])]});}
            extrude(context, id + "F19", {"entities" : qUnion([Q0, Q1]), "operationType" : NewBodyOperationType.ADD, "depth" : 620 * mm, "offsetDistance" : 25 * mm, "symmetric" : true});
        }
        {
            var Q0;
            {var subQ0=sQuery(id+"F3.wireOp",EDGE,"E163.MirrorCS");Q0=makeQuery(id+"F3.imprint","IMPRINT",FACE,{"disambiguationData":[TD([[makeQuery(id+"F3.imprint","IMPRINT",EDGE,{"derivedFrom":subQ0}),-1.0]])]});}
            var Q1;
            {var subQ0=sQuery(id+"F3.wireOp",EDGE,"E160");Q1=makeQuery(id+"F3.imprint","IMPRINT",FACE,{"disambiguationData":[TD([[makeQuery(id+"F3.imprint","IMPRINT",EDGE,{"derivedFrom":subQ0}),-1.0]])]});}
            extrude(context, id + "F20", {"entities" : qUnion([Q0, Q1]), "operationType" : NewBodyOperationType.ADD, "depth" : 620 * mm, "offsetDistance" : 25 * mm, "symmetric" : true});
        }
        {
            var Q0;
            Q0=makeQuery(id+"F5.opExtrude","CAP_EDGE",EDGE,{"disambiguationData":[OSD([sQuery(id+"F2.wireOp",EDGE,"E124.MirrorCS")])],"isStart":false});
            var Q1;
            Q1=makeQuery(id+"F5.opExtrude","CAP_EDGE",EDGE,{"disambiguationData":[OSD([sQuery(id+"F2.wireOp",EDGE,"E123.MirrorCS")])],"isStart":false});
            var Q2;
            Q2=makeQuery(id+"F5.opExtrude","CAP_EDGE",EDGE,{"disambiguationData":[OSD([sQuery(id+"F2.wireOp",EDGE,"E90.trimOffspring")])],"isStart":false});
            var Q3;
            Q3=makeQuery(id+"F5.opExtrude","CAP_EDGE",EDGE,{"disambiguationData":[OSD([sQuery(id+"F2.wireOp",EDGE,"E102.MirrorCS")])],"isStart":false});
            chamfer(context, id + "F21", {"entities" : qUnion([Q0, Q1, Q2, Q3]), "chamferType" : ChamferType.OFFSET_ANGLE, "width" : 15 * mm, "oppositeDirection" : false, "angle" : 35 * degree, "tangentPropagation" : true});
        }
        {
            var Q0;
            {var subQ0=sQuery(id+"F4.wireOp",EDGE,"E198.MirrorCS");var subQ1=sQuery(id+"F4.wireOp",EDGE,"E186.MirrorCS");var subQ2=sQuery(id+"F4.wireOp",EDGE,"E185.MirrorCS");Q0=makeQuery(id+"F11.boolean.opBoolean","MERGE",EDGE,{"derivedFrom":[makeQuery(id+"F8.opExtrude","SWEPT_EDGE",EDGE,{"disambiguationData":[OSD([subQ2,subQ1,subQ0])]}),makeQuery(id+"F11.opExtrude","SWEPT_EDGE",EDGE,{"disambiguationData":[OSD([subQ2,subQ1,subQ0])]})]});}
            chamfer(context, id + "F22", {"entities" : qUnion([Q0]), "chamferType" : ChamferType.OFFSET_ANGLE, "width" : 10 * mm, "oppositeDirection" : false, "angle" : 42 * degree, "tangentPropagation" : true});
        }
        {
            var Q0;
            {var subQ0=sQuery(id+"F4.wireOp",EDGE,"E196");var subQ1=sQuery(id+"F4.wireOp",EDGE,"E179");var subQ2=sQuery(id+"F4.wireOp",EDGE,"E174");Q0=makeQuery(id+"F11.boolean.opBoolean","MERGE",EDGE,{"derivedFrom":[makeQuery(id+"F8.opExtrude","SWEPT_EDGE",EDGE,{"disambiguationData":[OSD([subQ2,subQ1,subQ0])]}),makeQuery(id+"F11.opExtrude","SWEPT_EDGE",EDGE,{"disambiguationData":[OSD([subQ2,subQ1,subQ0])]})]});}
            chamfer(context, id + "F23", {"entities" : qUnion([Q0]), "chamferType" : ChamferType.OFFSET_ANGLE, "width" : 10 * mm, "oppositeDirection" : false, "angle" : 42 * degree, "tangentPropagation" : true});
        }
        {
            var Q0;
            {var subQ0=sQuery(id+"F0.wireOp",EDGE,"E35.top");var subQ1=sQuery(id+"F0.wireOp",EDGE,"E34.MirrorC");var subQ2=makeQuery(id+"F0.imprint","INTERSECT",VERTEX,{"derivedFrom":[subQ1,subQ0]});Q0=makeQuery(id+"F0.imprint","IMPRINT",FACE,{"disambiguationData":[TD([[makeQuery(id+"F0.imprint","IMPRINT",EDGE,{"disambiguationData":[TD([[subQ2,1.0]])],"derivedFrom":subQ1}),1.0]])]});}
            var Q1;
            {var subQ0=sQuery(id+"F0.wireOp",EDGE,"E10");var subQ3=sQuery(id+"F0.wireOp",EDGE,"E1");var subQ5=makeQuery(id+"F0.imprint","INTERSECT",VERTEX,{"disambiguationData":[OD(0.0)],"derivedFrom":[subQ3,subQ0]});Q1=makeQuery(id+"F0.imprint","IMPRINT",FACE,{"disambiguationData":[TD([[makeQuery(id+"F0.imprint","IMPRINT",EDGE,{"disambiguationData":[TD([[subQ5,-1.0]])],"derivedFrom":subQ3}),-1.0]])]});}
            var Q2;
            {var subQ0=sQuery(id+"F0.wireOp",EDGE,"E36");var subQ1=sQuery(id+"F0.wireOp",EDGE,"E0.right");var subQ2=makeQuery(id+"F0.imprint","INTERSECT",VERTEX,{"derivedFrom":[subQ1,subQ0]});Q2=makeQuery(id+"F0.imprint","IMPRINT",FACE,{"disambiguationData":[TD([[makeQuery(id+"F0.imprint","IMPRINT",EDGE,{"disambiguationData":[TD([[subQ2,1.0]])],"derivedFrom":subQ1}),-1.0]])]});}
            var Q3;
            {var subQ1=sQuery(id+"F0.wireOp",EDGE,"E0.left");var subQ3=sQuery(id+"F0.wireOp",EDGE,"E2.MirrorCS");var subQ4=makeQuery(id+"F0.imprint","INTERSECT",VERTEX,{"disambiguationData":[OD(1.0)],"derivedFrom":[subQ1,subQ3]});Q3=makeQuery(id+"F0.imprint","IMPRINT",FACE,{"disambiguationData":[TD([[makeQuery(id+"F0.imprint","IMPRINT",EDGE,{"disambiguationData":[TD([[subQ4,-1.0]])],"derivedFrom":subQ3}),-1.0]])]});}
            var Q4;
            {var subQ1=sQuery(id+"F0.wireOp",EDGE,"E0.left");var subQ3=sQuery(id+"F0.wireOp",EDGE,"E3.MirrorCS");var subQ4=makeQuery(id+"F0.imprint","INTERSECT",VERTEX,{"derivedFrom":[subQ1,subQ3]});Q4=makeQuery(id+"F0.imprint","IMPRINT",FACE,{"disambiguationData":[TD([[makeQuery(id+"F0.imprint","IMPRINT",EDGE,{"disambiguationData":[TD([[subQ4,1.0]])],"derivedFrom":subQ3}),-1.0]])]});}
            var Q5;
            {var subQ0=sQuery(id+"F0.wireOp",EDGE,"E9");var subQ1=sQuery(id+"F0.wireOp",EDGE,"E0.right");var subQ2=makeQuery(id+"F0.imprint","INTERSECT",VERTEX,{"derivedFrom":[subQ1,subQ0]});Q5=makeQuery(id+"F0.imprint","IMPRINT",FACE,{"disambiguationData":[TD([[makeQuery(id+"F0.imprint","IMPRINT",EDGE,{"disambiguationData":[TD([[subQ2,-1.0]])],"derivedFrom":subQ1}),-1.0]])]});}
            var Q6;
            Q6=makeQuery(id+"F0.imprint","IMPRINT",FACE,{"disambiguationData":[TD([[makeQuery(id+"F0.imprint","IMPRINT",EDGE,{"derivedFrom":sQuery(id+"F0.wireOp",EDGE,"E23")}),1.0]])]});
            var Q7;
            Q7=makeQuery(id+"F0.imprint","IMPRINT",FACE,{"disambiguationData":[TD([[makeQuery(id+"F0.imprint","IMPRINT",EDGE,{"derivedFrom":sQuery(id+"F0.wireOp",EDGE,"E21")}),1.0]])]});
            var Q8;
            Q8=makeQuery(id+"F0.imprint","IMPRINT",FACE,{"disambiguationData":[TD([[makeQuery(id+"F0.imprint","IMPRINT",EDGE,{"derivedFrom":sQuery(id+"F0.wireOp",EDGE,"E22")}),1.0]])]});
            var Q9;
            Q9=makeQuery(id+"F0.imprint","IMPRINT",FACE,{"disambiguationData":[TD([[makeQuery(id+"F0.imprint","IMPRINT",EDGE,{"derivedFrom":sQuery(id+"F0.wireOp",EDGE,"E24.MirrorC")}),-1.0]])]});
            var Q10;
            Q10=makeQuery(id+"F0.imprint","IMPRINT",FACE,{"disambiguationData":[TD([[makeQuery(id+"F0.imprint","IMPRINT",EDGE,{"derivedFrom":sQuery(id+"F0.wireOp",EDGE,"E30.MirrorC")}),-1.0]])]});
            var Q11;
            Q11=makeQuery(id+"F0.imprint","IMPRINT",FACE,{"disambiguationData":[TD([[makeQuery(id+"F0.imprint","IMPRINT",EDGE,{"derivedFrom":sQuery(id+"F0.wireOp",EDGE,"E31.MirrorC")}),-1.0]])]});
            var Q12;
            Q12=makeQuery(id+"F0.imprint","IMPRINT",FACE,{"disambiguationData":[TD([[makeQuery(id+"F0.imprint","IMPRINT",EDGE,{"derivedFrom":sQuery(id+"F0.wireOp",EDGE,"E33.MirrorC")}),1.0]])]});
            var Q13;
            Q13=makeQuery(id+"F0.imprint","IMPRINT",FACE,{"disambiguationData":[TD([[makeQuery(id+"F0.imprint","IMPRINT",EDGE,{"derivedFrom":sQuery(id+"F0.wireOp",EDGE,"E32.MirrorC")}),-1.0]])]});
            var Q14;
            Q14=makeQuery(id+"F0.imprint","IMPRINT",FACE,{"disambiguationData":[TD([[makeQuery(id+"F0.imprint","IMPRINT",EDGE,{"derivedFrom":sQuery(id+"F0.wireOp",EDGE,"E19")}),1.0]])]});
            var Q15;
            Q15=makeQuery(id+"F0.imprint","IMPRINT",FACE,{"disambiguationData":[TD([[makeQuery(id+"F0.imprint","IMPRINT",EDGE,{"derivedFrom":sQuery(id+"F0.wireOp",EDGE,"E20")}),1.0]])]});
            var Q16;
            Q16=makeQuery(id+"F0.imprint","IMPRINT",FACE,{"disambiguationData":[TD([[makeQuery(id+"F0.imprint","IMPRINT",EDGE,{"derivedFrom":sQuery(id+"F0.wireOp",EDGE,"E17")}),1.0]])]});
            var Q17;
            Q17=makeQuery(id+"F0.imprint","IMPRINT",FACE,{"disambiguationData":[TD([[makeQuery(id+"F0.imprint","IMPRINT",EDGE,{"derivedFrom":sQuery(id+"F0.wireOp",EDGE,"E18")}),1.0]])]});
            var Q18;
            Q18=makeQuery(id+"F0.imprint","IMPRINT",FACE,{"disambiguationData":[TD([[makeQuery(id+"F0.imprint","IMPRINT",EDGE,{"derivedFrom":sQuery(id+"F0.wireOp",EDGE,"E16")}),1.0]])]});
            var Q19;
            Q19=makeQuery(id+"F0.imprint","IMPRINT",FACE,{"disambiguationData":[TD([[makeQuery(id+"F0.imprint","IMPRINT",EDGE,{"derivedFrom":sQuery(id+"F0.wireOp",EDGE,"E28.MirrorC")}),-1.0]])]});
            var Q20;
            Q20=makeQuery(id+"F0.imprint","IMPRINT",FACE,{"disambiguationData":[TD([[makeQuery(id+"F0.imprint","IMPRINT",EDGE,{"derivedFrom":sQuery(id+"F0.wireOp",EDGE,"E27.MirrorC")}),-1.0]])]});
            var Q21;
            Q21=makeQuery(id+"F0.imprint","IMPRINT",FACE,{"disambiguationData":[TD([[makeQuery(id+"F0.imprint","IMPRINT",EDGE,{"derivedFrom":sQuery(id+"F0.wireOp",EDGE,"E25.MirrorC")}),-1.0]])]});
            var Q22;
            Q22=makeQuery(id+"F0.imprint","IMPRINT",FACE,{"disambiguationData":[TD([[makeQuery(id+"F0.imprint","IMPRINT",EDGE,{"derivedFrom":sQuery(id+"F0.wireOp",EDGE,"E26.MirrorC")}),-1.0]])]});
            var Q23;
            Q23=makeQuery(id+"F0.imprint","IMPRINT",FACE,{"disambiguationData":[TD([[makeQuery(id+"F0.imprint","IMPRINT",EDGE,{"derivedFrom":sQuery(id+"F0.wireOp",EDGE,"E29.MirrorC")}),-1.0]])]});
            var Q24;
            {var subQ5=sQuery(id+"F0.wireOp",EDGE,"E7");Q24=makeQuery(id+"F0.imprint","IMPRINT",FACE,{"disambiguationData":[TD([[makeQuery(id+"F0.imprint","IMPRINT",EDGE,{"derivedFrom":subQ5}),-1.0]])]});}
            var Q25;
            {var subQ0=sQuery(id+"F0.wireOp",EDGE,"E37");var subQ1=sQuery(id+"F0.wireOp",EDGE,"E0.right");var subQ2=makeQuery(id+"F0.imprint","INTERSECT",VERTEX,{"derivedFrom":[subQ1,subQ0]});Q25=makeQuery(id+"F0.imprint","IMPRINT",FACE,{"disambiguationData":[TD([[makeQuery(id+"F0.imprint","IMPRINT",EDGE,{"disambiguationData":[TD([[subQ2,-1.0]])],"derivedFrom":subQ1}),-1.0]])]});}
            var Q26;
            {var subQ5=sQuery(id+"F0.wireOp",EDGE,"E6");Q26=makeQuery(id+"F0.imprint","IMPRINT",FACE,{"disambiguationData":[TD([[makeQuery(id+"F0.imprint","IMPRINT",EDGE,{"derivedFrom":subQ5}),1.0]])]});}
            var Q27;
            Q27=makeQuery(id+"F0.imprint","IMPRINT",FACE,{"disambiguationData":[TD([[makeQuery(id+"F0.imprint","IMPRINT",EDGE,{"derivedFrom":sQuery(id+"F0.wireOp",EDGE,"E46.MirrorC")}),-1.0]])]});
            var Q28;
            Q28=makeQuery(id+"F0.imprint","IMPRINT",FACE,{"disambiguationData":[TD([[makeQuery(id+"F0.imprint","IMPRINT",EDGE,{"derivedFrom":sQuery(id+"F0.wireOp",EDGE,"E45")}),1.0]])]});
            var Q29;
            {var subQ0=sQuery(id+"F0.wireOp",EDGE,"E47.MirrorC");var subQ1=sQuery(id+"F0.wireOp",EDGE,"E35.top");var subQ2=makeQuery(id+"F0.imprint","INTERSECT",VERTEX,{"disambiguationData":[OD(0.0)],"derivedFrom":[subQ1,subQ0]});Q29=makeQuery(id+"F0.imprint","IMPRINT",FACE,{"disambiguationData":[TD([[makeQuery(id+"F0.imprint","IMPRINT",EDGE,{"disambiguationData":[TD([[subQ2,-1.0]])],"derivedFrom":subQ1}),1.0]])]});}
            var Q30;
            {var subQ0=sQuery(id+"F0.wireOp",EDGE,"E48.MirrorC");var subQ1=sQuery(id+"F0.wireOp",EDGE,"E35.bottom");var subQ2=makeQuery(id+"F0.imprint","INTERSECT",VERTEX,{"disambiguationData":[OD(0.0)],"derivedFrom":[subQ1,subQ0]});Q30=makeQuery(id+"F0.imprint","IMPRINT",FACE,{"disambiguationData":[TD([[makeQuery(id+"F0.imprint","IMPRINT",EDGE,{"disambiguationData":[TD([[subQ2,-1.0]])],"derivedFrom":subQ1}),-1.0]])]});}
            var Q31;
            {var subQ0=sQuery(id+"F0.wireOp",EDGE,"E49.MirrorC");var subQ1=sQuery(id+"F0.wireOp",EDGE,"E35.top");var subQ2=makeQuery(id+"F0.imprint","INTERSECT",VERTEX,{"disambiguationData":[OD(0.0)],"derivedFrom":[subQ1,subQ0]});Q31=makeQuery(id+"F0.imprint","IMPRINT",FACE,{"disambiguationData":[TD([[makeQuery(id+"F0.imprint","IMPRINT",EDGE,{"disambiguationData":[TD([[subQ2,-1.0]])],"derivedFrom":subQ1}),1.0]])]});}
            var Q32;
            {var subQ0=sQuery(id+"F0.wireOp",EDGE,"E50.MirrorC");var subQ1=sQuery(id+"F0.wireOp",EDGE,"E35.top");var subQ2=makeQuery(id+"F0.imprint","INTERSECT",VERTEX,{"disambiguationData":[OD(0.0)],"derivedFrom":[subQ1,subQ0]});Q32=makeQuery(id+"F0.imprint","IMPRINT",FACE,{"disambiguationData":[TD([[makeQuery(id+"F0.imprint","IMPRINT",EDGE,{"disambiguationData":[TD([[subQ2,-1.0]])],"derivedFrom":subQ1}),1.0]])]});}
            var Q33;
            {var subQ0=sQuery(id+"F0.wireOp",EDGE,"E52.MirrorC");var subQ1=sQuery(id+"F0.wireOp",EDGE,"E35.bottom");var subQ2=makeQuery(id+"F0.imprint","INTERSECT",VERTEX,{"disambiguationData":[OD(0.0)],"derivedFrom":[subQ1,subQ0]});Q33=makeQuery(id+"F0.imprint","IMPRINT",FACE,{"disambiguationData":[TD([[makeQuery(id+"F0.imprint","IMPRINT",EDGE,{"disambiguationData":[TD([[subQ2,-1.0]])],"derivedFrom":subQ1}),-1.0]])]});}
            var Q34;
            {var subQ0=sQuery(id+"F0.wireOp",EDGE,"E51.MirrorC");var subQ1=sQuery(id+"F0.wireOp",EDGE,"E35.top");var subQ2=makeQuery(id+"F0.imprint","INTERSECT",VERTEX,{"disambiguationData":[OD(0.0)],"derivedFrom":[subQ1,subQ0]});Q34=makeQuery(id+"F0.imprint","IMPRINT",FACE,{"disambiguationData":[TD([[makeQuery(id+"F0.imprint","IMPRINT",EDGE,{"disambiguationData":[TD([[subQ2,-1.0]])],"derivedFrom":subQ1}),1.0]])]});}
            var Q35;
            {var subQ0=sQuery(id+"F0.wireOp",EDGE,"E35.left");var subQ1=sQuery(id+"F0.wireOp",EDGE,"E35.top");var subQ2=makeQuery(id+"F0.imprint","INTERSECT",VERTEX,{"derivedFrom":[subQ1,subQ0]});Q35=makeQuery(id+"F0.imprint","IMPRINT",FACE,{"disambiguationData":[TD([[makeQuery(id+"F0.imprint","IMPRINT",EDGE,{"disambiguationData":[TD([[subQ2,-1.0]])],"derivedFrom":subQ1}),1.0]])]});}
            var Q36;
            Q36=makeQuery(id+"F0.imprint","IMPRINT",FACE,{"disambiguationData":[TD([[makeQuery(id+"F0.imprint","IMPRINT",EDGE,{"derivedFrom":sQuery(id+"F0.wireOp",EDGE,"E54.MirrorC")}),-1.0]])]});
            var Q37;
            Q37=makeQuery(id+"F0.imprint","IMPRINT",FACE,{"disambiguationData":[TD([[makeQuery(id+"F0.imprint","IMPRINT",EDGE,{"derivedFrom":sQuery(id+"F0.wireOp",EDGE,"E55.MirrorC")}),1.0]])]});
            var Q38;
            Q38=makeQuery(id+"F0.imprint","IMPRINT",FACE,{"disambiguationData":[TD([[makeQuery(id+"F0.imprint","IMPRINT",EDGE,{"derivedFrom":sQuery(id+"F0.wireOp",EDGE,"E64.MirrorC")}),-1.0]])]});
            var Q39;
            Q39=makeQuery(id+"F0.imprint","IMPRINT",FACE,{"disambiguationData":[TD([[makeQuery(id+"F0.imprint","IMPRINT",EDGE,{"derivedFrom":sQuery(id+"F0.wireOp",EDGE,"E63.MirrorC")}),1.0]])]});
            var Q40;
            Q40=makeQuery(id+"F0.imprint","IMPRINT",FACE,{"disambiguationData":[TD([[makeQuery(id+"F0.imprint","IMPRINT",EDGE,{"derivedFrom":sQuery(id+"F0.wireOp",EDGE,"E62.MirrorC")}),1.0]])]});
            var Q41;
            Q41=makeQuery(id+"F0.imprint","IMPRINT",FACE,{"disambiguationData":[TD([[makeQuery(id+"F0.imprint","IMPRINT",EDGE,{"derivedFrom":sQuery(id+"F0.wireOp",EDGE,"E61.MirrorC")}),1.0]])]});
            var Q42;
            Q42=makeQuery(id+"F0.imprint","IMPRINT",FACE,{"disambiguationData":[TD([[makeQuery(id+"F0.imprint","IMPRINT",EDGE,{"derivedFrom":sQuery(id+"F0.wireOp",EDGE,"E60.MirrorC")}),1.0]])]});
            var Q43;
            Q43=makeQuery(id+"F0.imprint","IMPRINT",FACE,{"disambiguationData":[TD([[makeQuery(id+"F0.imprint","IMPRINT",EDGE,{"derivedFrom":sQuery(id+"F0.wireOp",EDGE,"E59.MirrorC")}),1.0]])]});
            var Q44;
            Q44=makeQuery(id+"F0.imprint","IMPRINT",FACE,{"disambiguationData":[TD([[makeQuery(id+"F0.imprint","IMPRINT",EDGE,{"derivedFrom":sQuery(id+"F0.wireOp",EDGE,"E57.MirrorC")}),1.0]])]});
            var Q45;
            Q45=makeQuery(id+"F0.imprint","IMPRINT",FACE,{"disambiguationData":[TD([[makeQuery(id+"F0.imprint","IMPRINT",EDGE,{"derivedFrom":sQuery(id+"F0.wireOp",EDGE,"E56.MirrorC")}),1.0]])]});
            var Q46;
            Q46=makeQuery(id+"F0.imprint","IMPRINT",FACE,{"disambiguationData":[TD([[makeQuery(id+"F0.imprint","IMPRINT",EDGE,{"derivedFrom":sQuery(id+"F0.wireOp",EDGE,"E58.MirrorC")}),1.0]])]});
            var Q47;
            Q47=makeQuery(id+"F0.imprint","IMPRINT",FACE,{"disambiguationData":[TD([[makeQuery(id+"F0.imprint","IMPRINT",EDGE,{"derivedFrom":sQuery(id+"F0.wireOp",EDGE,"E69.MirrorC")}),-1.0]])]});
            var Q48;
            Q48=makeQuery(id+"F0.imprint","IMPRINT",FACE,{"disambiguationData":[TD([[makeQuery(id+"F0.imprint","IMPRINT",EDGE,{"derivedFrom":sQuery(id+"F0.wireOp",EDGE,"E68.MirrorC")}),-1.0]])]});
            var Q49;
            Q49=makeQuery(id+"F0.imprint","IMPRINT",FACE,{"disambiguationData":[TD([[makeQuery(id+"F0.imprint","IMPRINT",EDGE,{"derivedFrom":sQuery(id+"F0.wireOp",EDGE,"E70.MirrorC")}),-1.0]])]});
            var Q50;
            Q50=makeQuery(id+"F0.imprint","IMPRINT",FACE,{"disambiguationData":[TD([[makeQuery(id+"F0.imprint","IMPRINT",EDGE,{"derivedFrom":sQuery(id+"F0.wireOp",EDGE,"E67.MirrorC")}),-1.0]])]});
            var Q51;
            Q51=makeQuery(id+"F0.imprint","IMPRINT",FACE,{"disambiguationData":[TD([[makeQuery(id+"F0.imprint","IMPRINT",EDGE,{"derivedFrom":sQuery(id+"F0.wireOp",EDGE,"E71.MirrorC")}),-1.0]])]});
            var Q52;
            Q52=makeQuery(id+"F0.imprint","IMPRINT",FACE,{"disambiguationData":[TD([[makeQuery(id+"F0.imprint","IMPRINT",EDGE,{"derivedFrom":sQuery(id+"F0.wireOp",EDGE,"E72.MirrorC")}),-1.0]])]});
            var Q53;
            Q53=makeQuery(id+"F0.imprint","IMPRINT",FACE,{"disambiguationData":[TD([[makeQuery(id+"F0.imprint","IMPRINT",EDGE,{"derivedFrom":sQuery(id+"F0.wireOp",EDGE,"E66.MirrorC")}),-1.0]])]});
            var Q54;
            Q54=makeQuery(id+"F0.imprint","IMPRINT",FACE,{"disambiguationData":[TD([[makeQuery(id+"F0.imprint","IMPRINT",EDGE,{"derivedFrom":sQuery(id+"F0.wireOp",EDGE,"E65.MirrorC")}),-1.0]])]});
            var Q55;
            Q55=makeQuery(id+"F0.imprint","IMPRINT",FACE,{"disambiguationData":[TD([[makeQuery(id+"F0.imprint","IMPRINT",EDGE,{"derivedFrom":sQuery(id+"F0.wireOp",EDGE,"E73.MirrorC")}),1.0]])]});
            extrude(context, id + "F24", {"entities" : qUnion([Q0, Q1, Q2, Q3, Q4, Q5, Q6, Q7, Q8, Q9, Q10, Q11, Q12, Q13, Q14, Q15, Q16, Q17, Q18, Q19, Q20, Q21, Q22, Q23, Q24, Q25, Q26, Q27, Q28, Q29, Q30, Q31, Q32, Q33, Q34, Q35, Q36, Q37, Q38, Q39, Q40, Q41, Q42, Q43, Q44, Q45, Q46, Q47, Q48, Q49, Q50, Q51, Q52, Q53, Q54, Q55]), "operationType" : NewBodyOperationType.REMOVE, "depth" : 25 * mm, "offsetDistance" : 25 * mm});
        }
        {
            var Q0;
            Q0=qCreatedBy(makeId("Top.planeOp"),FACE);
            var sketch = newSketch(context, id + "F25", { "sketchPlane" : qUnion([Q0])});
            skLineSegment(sketch, "E212.bottom", {"start": v(-365, -200) * mm, "end": v(365, -200) * mm});
            skLineSegment(sketch, "E212.top", {"start": v(-365, 200) * mm, "end": v(365, 200) * mm});
            skLineSegment(sketch, "E212.left", {"start": v(-365, -200) * mm, "end": v(-365, 200) * mm});
            skLineSegment(sketch, "E212.right", {"start": v(365, -200) * mm, "end": v(365, 200) * mm});
            skPoint(sketch, "E212.middle", {"position": v(0, 0) * mm});
            skPoint(sketch, "E213", {"position": v(-182.5, -200) * mm});
            skPoint(sketch, "E214", {"position": v(-182.5, 200) * mm});
            skPoint(sketch, "E215", {"position": v(-365, -50) * mm});
            skPoint(sketch, "E216", {"position": v(0, -50) * mm});
            skPoint(sketch, "E217", {"position": v(-182.5, 0) * mm});
            skPoint(sketch, "E218", {"position": v(-192.5, -200) * mm});
            skPoint(sketch, "E219", {"position": v(-172.5, -200) * mm});
            skPoint(sketch, "E220", {"position": v(-365, -60) * mm});
            skPoint(sketch, "E221", {"position": v(-365, -39.93) * mm});
            skPoint(sketch, "E222", {"position": v(-10, -200) * mm});
            skPoint(sketch, "E223", {"position": v(-321.88, -49.93) * mm});
            skPoint(sketch, "E224", {"position": v(-278.75, -49.93) * mm});
            skPoint(sketch, "E225", {"position": v(-235.63, -50) * mm});
            skPoint(sketch, "E226.MirrorP", {"position": v(-131.88, -49.93) * mm});
            skPoint(sketch, "E227.MirrorP", {"position": v(-91.25, -49.93) * mm});
            skPoint(sketch, "E228.MirrorP", {"position": v(-50.63, -50) * mm});
            skPoint(sketch, "E229", {"position": v(-182.5, -20) * mm});
            skPoint(sketch, "E230", {"position": v(-182.5, -95) * mm});
            skPoint(sketch, "E231", {"position": v(-182.5, -130) * mm});
            skPoint(sketch, "E232", {"position": v(-182.5, -165) * mm});
            skLineSegment(sketch, "E233", {"start": v(-365, -39.93) * mm, "end": v(-321.88, -39.93) * mm});
            skLineSegment(sketch, "E234", {"start": v(-321.88, -39.93) * mm, "end": v(-321.88, -59.93) * mm});
            skLineSegment(sketch, "E235", {"start": v(-321.88, -59.93) * mm, "end": v(-278.75, -59.93) * mm});
            skLineSegment(sketch, "E236", {"start": v(-278.75, -59.93) * mm, "end": v(-278.75, -39.93) * mm});
            skLineSegment(sketch, "E237", {"start": v(-278.75, -39.93) * mm, "end": v(-235.63, -39.93) * mm});
            skLineSegment(sketch, "E238", {"start": v(-235.62, -39.93) * mm, "end": v(-235.62, -59.93) * mm});
            skLineSegment(sketch, "E239", {"start": v(-235.62, -59.93) * mm, "end": v(-192.5, -59.93) * mm});
            skLineSegment(sketch, "E240", {"start": v(-192.5, -59.93) * mm, "end": v(-192.5, -50) * mm});
            skLineSegment(sketch, "E241", {"start": v(-192.5, -50) * mm, "end": v(-172.5, -50) * mm});
            skLineSegment(sketch, "E242", {"start": v(-172.5, -50) * mm, "end": v(-172.5, -39.93) * mm});
            skLineSegment(sketch, "E243", {"start": v(-192.5, -40) * mm, "end": v(-182.5, -40) * mm});
            skPoint(sketch, "E243.startSnap0", {"position": v(-182.5, -40) * mm});
            skLineSegment(sketch, "E244", {"start": v(-182.5, -40) * mm, "end": v(-182.5, -60) * mm});
            skLineSegment(sketch, "E245", {"start": v(-182.5, -60) * mm, "end": v(-172.5, -60) * mm});
            skLineSegment(sketch, "E246", {"start": v(-172.5, -60) * mm, "end": v(-172.5, -95) * mm});
            skLineSegment(sketch, "E247", {"start": v(-172.5, -95) * mm, "end": v(-192.5, -95) * mm});
            skLineSegment(sketch, "E248", {"start": v(-192.5, -95) * mm, "end": v(-192.5, -130) * mm});
            skLineSegment(sketch, "E249", {"start": v(-192.5, -130) * mm, "end": v(-172.5, -130) * mm});
            skLineSegment(sketch, "E250", {"start": v(-172.5, -130) * mm, "end": v(-172.5, -165) * mm});
            skLineSegment(sketch, "E251", {"start": v(-172.5, -165) * mm, "end": v(-192.5, -165) * mm});
            skLineSegment(sketch, "E252", {"start": v(-192.5, -165) * mm, "end": v(-192.5, -200) * mm});
            skLineSegment(sketch, "E253", {"start": v(-192.5, -40) * mm, "end": v(-192.5, -20) * mm});
            skLineSegment(sketch, "E254", {"start": v(-192.5, -20) * mm, "end": v(-172.5, -20) * mm});
            skLineSegment(sketch, "E255", {"start": v(-172.5, -20) * mm, "end": v(-172.5, 0) * mm});
            skPoint(sketch, "E256", {"position": v(0, -165) * mm});
            skPoint(sketch, "E257", {"position": v(0, -130) * mm});
            skPoint(sketch, "E258", {"position": v(0, -95) * mm});
            skPoint(sketch, "E259", {"position": v(0, -20) * mm});
            skPoint(sketch, "E260.MirrorP", {"position": v(182.5, -165) * mm});
            skPoint(sketch, "E261.MirrorP", {"position": v(182.5, -130) * mm});
            skPoint(sketch, "E262.MirrorP", {"position": v(182.5, -95) * mm});
            skPoint(sketch, "E263.MirrorP", {"position": v(182.5, -20) * mm});
            skPoint(sketch, "E264.MirrorP", {"position": v(50.62, -50) * mm});
            skPoint(sketch, "E265.MirrorP", {"position": v(91.25, -50) * mm});
            skPoint(sketch, "E266.MirrorP", {"position": v(131.87, -50) * mm});
            skPoint(sketch, "E267.MirrorP", {"position": v(235.62, -50) * mm});
            skPoint(sketch, "E268.MirrorP", {"position": v(278.75, -50) * mm});
            skPoint(sketch, "E269.MirrorP", {"position": v(321.87, -50) * mm});
            skPoint(sketch, "E270.MirrorP", {"position": v(-321.88, 50) * mm});
            skPoint(sketch, "E271.MirrorP", {"position": v(-278.75, 50) * mm});
            skPoint(sketch, "E272.MirrorP", {"position": v(-235.62, 50) * mm});
            skPoint(sketch, "E273.MirrorP", {"position": v(-182.5, 20) * mm});
            skPoint(sketch, "E274.MirrorP", {"position": v(-182.5, 95) * mm});
            skPoint(sketch, "E275.MirrorP", {"position": v(-182.5, 130) * mm});
            skPoint(sketch, "E276.MirrorP", {"position": v(-182.5, 165) * mm});
            skPoint(sketch, "E277.MirrorP", {"position": v(-131.88, 50) * mm});
            skPoint(sketch, "E278.MirrorP", {"position": v(-91.25, 50.16) * mm});
            skPoint(sketch, "E279.MirrorP", {"position": v(-50.63, 50) * mm});
            skPoint(sketch, "E280.MirrorP", {"position": v(0, 20) * mm});
            skPoint(sketch, "E281.MirrorP", {"position": v(0, 95) * mm});
            skPoint(sketch, "E282.MirrorP", {"position": v(0, 130) * mm});
            skPoint(sketch, "E283.MirrorP", {"position": v(0, 165) * mm});
            skPoint(sketch, "E284.MirrorP", {"position": v(43.13, 50) * mm});
            skPoint(sketch, "E285.MirrorP", {"position": v(86.25, 50) * mm});
            skPoint(sketch, "E286.MirrorP", {"position": v(129.38, 50) * mm});
            skPoint(sketch, "E287.MirrorP", {"position": v(182.5, 95) * mm});
            skPoint(sketch, "E288.MirrorP", {"position": v(182.5, 130) * mm});
            skPoint(sketch, "E289.MirrorP", {"position": v(182.5, 165) * mm});
            skPoint(sketch, "E290.MirrorP", {"position": v(182.5, 20) * mm});
            skPoint(sketch, "E291.MirrorP", {"position": v(235.62, 50) * mm});
            skPoint(sketch, "E292.MirrorP", {"position": v(278.75, 50) * mm});
            skPoint(sketch, "E293.MirrorP", {"position": v(321.88, 50) * mm});
            skLineSegment(sketch, "E294", {"start": v(-192.5, 0) * mm, "end": v(-192.5, 20) * mm});
            skLineSegment(sketch, "E295", {"start": v(-192.5, 20) * mm, "end": v(-172.5, 20) * mm});
            skLineSegment(sketch, "E296", {"start": v(-172.5, 20) * mm, "end": v(-172.5, 40) * mm});
            skLineSegment(sketch, "E297", {"start": v(-172.5, 40) * mm, "end": v(-182.5, 40) * mm});
            skLineSegment(sketch, "E298", {"start": v(-182.5, 40) * mm, "end": v(-182.5, 50) * mm});
            skPoint(sketch, "E298.endSnap0", {"position": v(-182.5, 60) * mm});
            skLineSegment(sketch, "E299", {"start": v(-182.5, 50) * mm, "end": v(-192.5, 50) * mm});
            skLineSegment(sketch, "E300", {"start": v(-192.5, 50) * mm, "end": v(-192.5, 40) * mm});
            skLineSegment(sketch, "E301", {"start": v(-192.5, 40) * mm, "end": v(-235.62, 40) * mm});
            skLineSegment(sketch, "E302", {"start": v(-235.62, 40) * mm, "end": v(-235.62, 60) * mm});
            skLineSegment(sketch, "E303", {"start": v(-235.62, 60) * mm, "end": v(-278.75, 60) * mm});
            skLineSegment(sketch, "E304", {"start": v(-278.75, 60) * mm, "end": v(-278.75, 40) * mm});
            skLineSegment(sketch, "E305", {"start": v(-278.75, 40) * mm, "end": v(-321.88, 40) * mm});
            skLineSegment(sketch, "E306", {"start": v(-321.88, 40) * mm, "end": v(-321.88, 60) * mm});
            skLineSegment(sketch, "E307", {"start": v(-321.88, 60) * mm, "end": v(-365, 60) * mm});
            skLineSegment(sketch, "E308", {"start": v(-182.5, 50) * mm, "end": v(-172.5, 50) * mm});
            skLineSegment(sketch, "E309", {"start": v(-172.5, 50) * mm, "end": v(-172.5, 60) * mm});
            skLineSegment(sketch, "E310", {"start": v(-172.5, 60) * mm, "end": v(-131.88, 60) * mm});
            skLineSegment(sketch, "E311", {"start": v(-131.88, 60) * mm, "end": v(-131.88, 40) * mm});
            skLineSegment(sketch, "E312", {"start": v(-131.88, 40) * mm, "end": v(-91.25, 40) * mm});
            skLineSegment(sketch, "E313", {"start": v(-91.25, 40) * mm, "end": v(-91.25, 60) * mm});
            skLineSegment(sketch, "E314", {"start": v(-91.25, 60) * mm, "end": v(-50.63, 60) * mm});
            skLineSegment(sketch, "E315", {"start": v(-50.63, 60) * mm, "end": v(-50.63, 40) * mm});
            skLineSegment(sketch, "E316", {"start": v(-50.63, 40) * mm, "end": v(-10, 40) * mm});
            skLineSegment(sketch, "E317", {"start": v(-10, 40) * mm, "end": v(-10, 50) * mm});
            skLineSegment(sketch, "E318", {"start": v(-10, 50) * mm, "end": v(0, 50) * mm});
            skLineSegment(sketch, "E319", {"start": v(0, 50) * mm, "end": v(0, 40) * mm});
            skLineSegment(sketch, "E320", {"start": v(10, 40) * mm, "end": v(10, 20) * mm});
            skLineSegment(sketch, "E321", {"start": v(10, 20) * mm, "end": v(-10, 20) * mm});
            skLineSegment(sketch, "E322", {"start": v(-10, 20) * mm, "end": v(-10, 0) * mm});
            skLineSegment(sketch, "E323", {"start": v(10, 0) * mm, "end": v(10, -20) * mm});
            skLineSegment(sketch, "E324", {"start": v(10, -20) * mm, "end": v(-10, -20) * mm});
            skLineSegment(sketch, "E325", {"start": v(-10, -20) * mm, "end": v(-10, -39.95) * mm});
            skLineSegment(sketch, "E326", {"start": v(-10, -39.95) * mm, "end": v(0, -39.95) * mm});
            skLineSegment(sketch, "E327", {"start": v(0, -59.93) * mm, "end": v(10, -59.93) * mm});
            skLineSegment(sketch, "E328", {"start": v(10, -59.93) * mm, "end": v(10, -95) * mm});
            skLineSegment(sketch, "E329", {"start": v(10, -95) * mm, "end": v(-10, -95) * mm});
            skLineSegment(sketch, "E330", {"start": v(-10, -95) * mm, "end": v(-10, -130.37) * mm});
            skLineSegment(sketch, "E331", {"start": v(-10, -130.37) * mm, "end": v(10, -130.37) * mm});
            skLineSegment(sketch, "E332", {"start": v(10, -130.37) * mm, "end": v(10, -165.52) * mm});
            skLineSegment(sketch, "E333", {"start": v(10, -165.52) * mm, "end": v(-10, -165.52) * mm});
            skLineSegment(sketch, "E334", {"start": v(-10, -165.52) * mm, "end": v(-10, -200) * mm});
            skPoint(sketch, "E335.orphan", {"position": v(-10, 60) * mm});
            skLineSegment(sketch, "E336", {"start": v(0, 40) * mm, "end": v(10, 40) * mm});
            skLineSegment(sketch, "E337", {"start": v(-172.5, -39.93) * mm, "end": v(-131.88, -39.93) * mm});
            skLineSegment(sketch, "E338", {"start": v(-131.88, -39.93) * mm, "end": v(-131.88, -59.93) * mm});
            skLineSegment(sketch, "E339", {"start": v(-131.88, -59.93) * mm, "end": v(-91.25, -59.93) * mm});
            skLineSegment(sketch, "E340", {"start": v(-91.25, -59.93) * mm, "end": v(-91.25, -39.93) * mm});
            skLineSegment(sketch, "E341", {"start": v(-91.25, -39.93) * mm, "end": v(-50.63, -39.93) * mm});
            skLineSegment(sketch, "E342", {"start": v(-50.63, -39.93) * mm, "end": v(-50.63, -59.93) * mm});
            skLineSegment(sketch, "E343", {"start": v(0, -59.93) * mm, "end": v(0, -49.93) * mm});
            skLineSegment(sketch, "E344", {"start": v(0, -49.93) * mm, "end": v(10, -49.93) * mm});
            skLineSegment(sketch, "E345", {"start": v(10, -49.93) * mm, "end": v(10, -39.93) * mm});
            skLineSegment(sketch, "E346", {"start": v(10, -39.93) * mm, "end": v(50.62, -39.93) * mm});
            skLineSegment(sketch, "E347", {"start": v(50.62, -39.93) * mm, "end": v(50.62, -59.93) * mm});
            skLineSegment(sketch, "E348", {"start": v(50.62, -59.93) * mm, "end": v(91.25, -59.93) * mm});
            skLineSegment(sketch, "E349", {"start": v(91.25, -59.93) * mm, "end": v(91.25, -39.93) * mm});
            skLineSegment(sketch, "E350", {"start": v(91.25, -39.93) * mm, "end": v(131.87, -39.93) * mm});
            skLineSegment(sketch, "E351", {"start": v(131.88, -39.93) * mm, "end": v(131.88, -59.93) * mm});
            skLineSegment(sketch, "E352", {"start": v(131.87, -59.93) * mm, "end": v(172.5, -59.93) * mm});
            skLineSegment(sketch, "E353", {"start": v(172.5, -59.93) * mm, "end": v(172.5, -49.93) * mm});
            skLineSegment(sketch, "E354", {"start": v(172.5, -49.93) * mm, "end": v(192.5, -49.93) * mm});
            skLineSegment(sketch, "E355", {"start": v(192.5, -49.93) * mm, "end": v(192.5, -39.93) * mm});
            skLineSegment(sketch, "E356", {"start": v(192.5, -39.93) * mm, "end": v(235.62, -39.93) * mm});
            skLineSegment(sketch, "E357", {"start": v(235.62, -39.93) * mm, "end": v(235.62, -59.93) * mm});
            skLineSegment(sketch, "E358", {"start": v(235.62, -59.93) * mm, "end": v(278.75, -59.93) * mm});
            skLineSegment(sketch, "E359", {"start": v(278.75, -59.93) * mm, "end": v(278.75, -39.93) * mm});
            skLineSegment(sketch, "E360", {"start": v(278.75, -39.93) * mm, "end": v(321.87, -39.93) * mm});
            skLineSegment(sketch, "E361", {"start": v(321.87, -39.93) * mm, "end": v(321.87, -59.93) * mm});
            skLineSegment(sketch, "E362", {"start": v(321.87, -59.93) * mm, "end": v(365, -59.93) * mm});
            skLineSegment(sketch, "E363", {"start": v(0, -40) * mm, "end": v(0, -60) * mm});
            skLineSegment(sketch, "E364", {"start": v(182.5, -49.93) * mm, "end": v(182.5, -59.93) * mm});
            skLineSegment(sketch, "E365", {"start": v(182.5, -59.93) * mm, "end": v(192.5, -59.93) * mm});
            skLineSegment(sketch, "E366", {"start": v(192.5, -59.93) * mm, "end": v(192.5, -95) * mm});
            skLineSegment(sketch, "E367", {"start": v(192.5, -95) * mm, "end": v(172.5, -95) * mm});
            skLineSegment(sketch, "E368", {"start": v(172.5, -95) * mm, "end": v(172.5, -130) * mm});
            skLineSegment(sketch, "E369", {"start": v(172.5, -130) * mm, "end": v(192.5, -130) * mm});
            skLineSegment(sketch, "E370", {"start": v(192.5, -130) * mm, "end": v(192.5, -165) * mm});
            skLineSegment(sketch, "E371", {"start": v(192.5, -165) * mm, "end": v(172.5, -165) * mm});
            skLineSegment(sketch, "E372", {"start": v(172.5, -165) * mm, "end": v(172.5, -200) * mm});
            skLineSegment(sketch, "E373", {"start": v(-192.5, 0) * mm, "end": v(-172.5, 0) * mm});
            skLineSegment(sketch, "E374", {"start": v(-10, 0) * mm, "end": v(10, 0) * mm});
            skLineSegment(sketch, "E375", {"start": v(0, -50) * mm, "end": v(-10, -50) * mm});
            skLineSegment(sketch, "E376", {"start": v(-10, -50) * mm, "end": v(-10, -60) * mm});
            skLineSegment(sketch, "E377", {"start": v(-10, -60) * mm, "end": v(-50.63, -59.93) * mm});
            skSolve(sketch);
        }
        {
            var Q0;
            Q0=qCreatedBy(makeId("Right.planeOp"),FACE);
            cPlane(context, id + "F26", {"entities" : qUnion([Q0]), "cplaneType" : CPlaneType.OFFSET, "offset" : 182.5 * mm, "width" : 150 * mm, "height" : 150 * mm});
        }
        {
            var Q0;
            Q0=qCreatedBy(makeId("Front.planeOp"),FACE);
            cPlane(context, id + "F27", {"entities" : qUnion([Q0]), "cplaneType" : CPlaneType.OFFSET, "offset" : 50 * mm, "width" : 150 * mm, "height" : 150 * mm});
        }
        {
            var Q0;
            Q0=qCreatedBy(makeId("Right.planeOp"),FACE);
            cPlane(context, id + "F28", {"entities" : qUnion([Q0]), "cplaneType" : CPlaneType.OFFSET, "offset" : 182.5 * mm, "oppositeDirection" : true, "width" : 150 * mm, "height" : 150 * mm});
        }
        {
            var Q0;
            Q0=qCreatedBy(makeId("Front.planeOp"),FACE);
            cPlane(context, id + "F29", {"entities" : qUnion([Q0]), "cplaneType" : CPlaneType.OFFSET, "offset" : 50 * mm, "oppositeDirection" : true, "width" : 150 * mm, "height" : 150 * mm});
        }
    });
